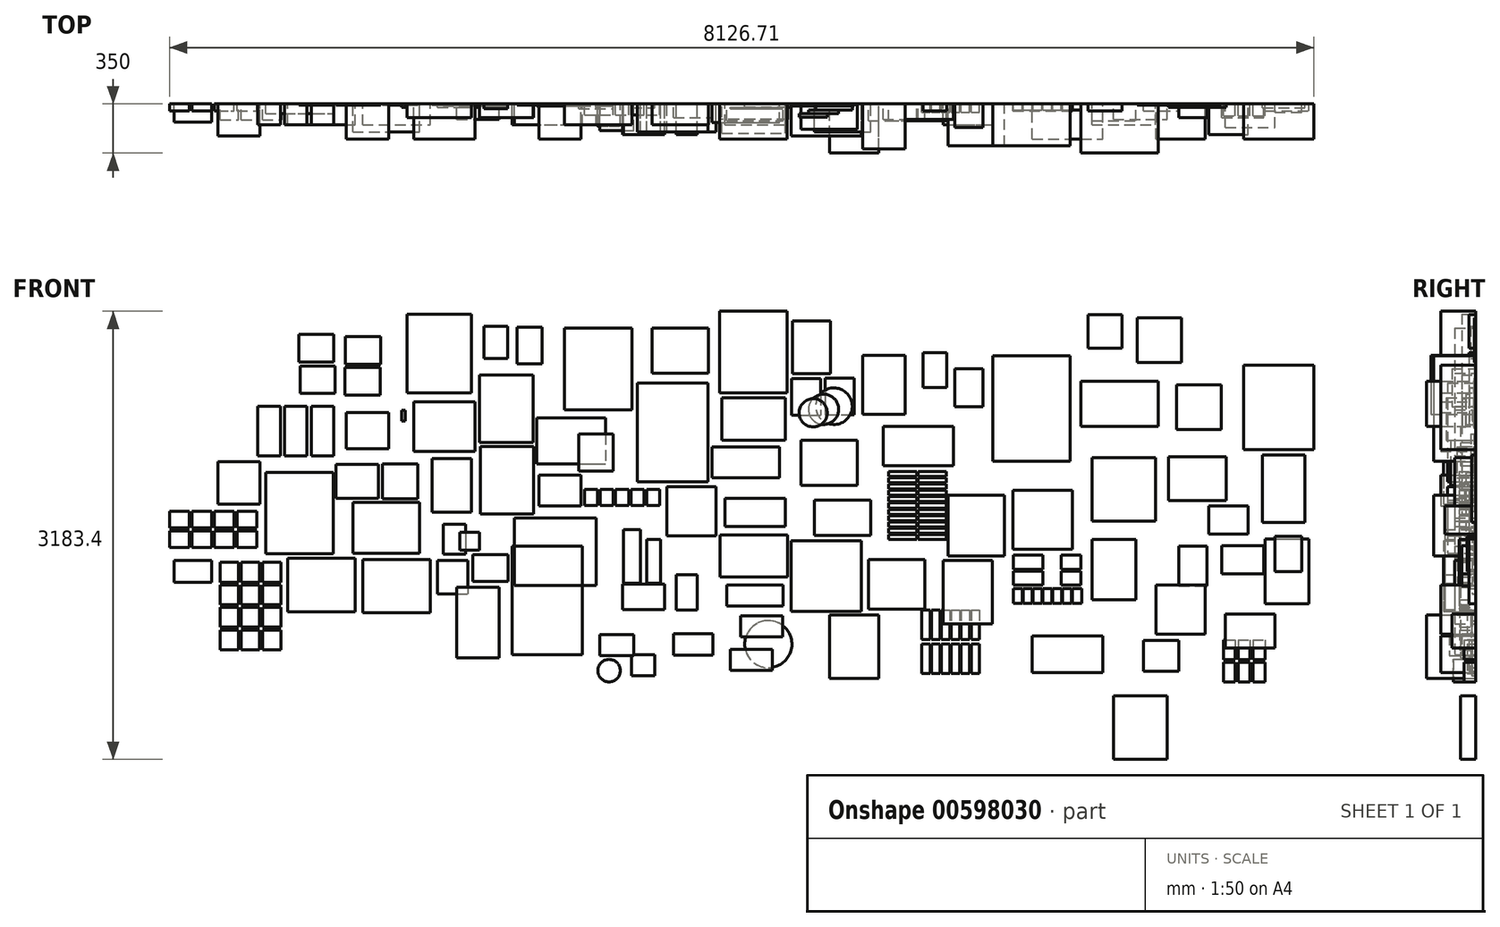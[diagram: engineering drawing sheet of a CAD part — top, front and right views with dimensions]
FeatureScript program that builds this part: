
annotation { "Feature Type Name" : "Feature", "Feature Type Description" : "" }
export const myFeature = defineFeature(function(context is Context, id is Id, definition is map)
    precondition{}
    {
        {
            var Q0;
            Q0=qCreatedBy(makeId("Front.planeOp"),FACE);
            var sketch = newSketch(context, id + "F0", { "sketchPlane" : qUnion([Q0])});
            skLineSegment(sketch, "E0.bottom", {"start": v(-280.76, 501.47) * mm, "end": v(269.24, 501.47) * mm});
            skLineSegment(sketch, "E0.top", {"start": v(-280.76, -248.53) * mm, "end": v(269.24, -248.53) * mm});
            skLineSegment(sketch, "E0.left", {"start": v(-280.76, 501.47) * mm, "end": v(-280.76, -248.53) * mm});
            skLineSegment(sketch, "E0.right", {"start": v(269.24, 501.47) * mm, "end": v(269.24, -248.53) * mm});
            skSolve(sketch);
        }
        {
            var Q0;
            Q0 = qSketchRegion(id + "F0", true);
            extrude(context, id + "F1", {"entities" : qUnion([Q0]), "depth" : 300 * mm, "offsetDistance" : 25 * mm});
        }
        {
            var Q0;
            Q0=qCreatedBy(makeId("Front.planeOp"),FACE);
            var sketch = newSketch(context, id + "F2", { "sketchPlane" : qUnion([Q0])});
            skLineSegment(sketch, "E1.bottom", {"start": v(-1059.28, 0) * mm, "end": v(-559.28, 0) * mm});
            skLineSegment(sketch, "E1.top", {"start": v(-1059.28, -280) * mm, "end": v(-559.28, -280) * mm});
            skLineSegment(sketch, "E1.left", {"start": v(-1059.28, 0) * mm, "end": v(-1059.28, -280) * mm});
            skLineSegment(sketch, "E1.right", {"start": v(-559.28, 0) * mm, "end": v(-559.28, -280) * mm});
            skSolve(sketch);
        }
        {
            var Q0;
            Q0=makeQuery(id+"F2.imprint","IMPRINT",FACE,{"disambiguationData":[TD([[makeQuery(id+"F2.imprint","IMPRINT",EDGE,{"derivedFrom":sQuery(id+"F2.wireOp",EDGE,"E1.bottom")}),-1.0]])]});
            extrude(context, id + "F3", {"entities" : qUnion([Q0]), "depth" : 110 * mm, "offsetDistance" : 25 * mm});
        }
        {
            var Q0;
            Q0=qCreatedBy(makeId("Front.planeOp"),FACE);
            var sketch = newSketch(context, id + "F4", { "sketchPlane" : qUnion([Q0])});
            skLineSegment(sketch, "E2.bottom", {"start": v(-1020.74, -769.84) * mm, "end": v(-820.74, -769.84) * mm});
            skLineSegment(sketch, "E2.top", {"start": v(-1020.74, -804.84) * mm, "end": v(-820.74, -804.84) * mm});
            skLineSegment(sketch, "E2.left", {"start": v(-1020.74, -769.84) * mm, "end": v(-1020.74, -804.84) * mm});
            skLineSegment(sketch, "E2.right", {"start": v(-820.74, -769.84) * mm, "end": v(-820.74, -804.84) * mm});
            skLineSegment(sketch, "E3.0.1.0", {"start": v(-1020.74, -724.84) * mm, "end": v(-1020.74, -759.84) * mm});
            skLineSegment(sketch, "E3.0.1.1", {"start": v(-1020.74, -759.84) * mm, "end": v(-820.74, -759.84) * mm});
            skLineSegment(sketch, "E3.0.1.2", {"start": v(-1020.74, -724.84) * mm, "end": v(-820.74, -724.84) * mm});
            skLineSegment(sketch, "E3.0.1.3", {"start": v(-820.74, -724.84) * mm, "end": v(-820.74, -759.84) * mm});
            skLineSegment(sketch, "E3.0.2.0", {"start": v(-1020.74, -679.84) * mm, "end": v(-1020.74, -714.84) * mm});
            skLineSegment(sketch, "E3.0.2.1", {"start": v(-1020.74, -714.84) * mm, "end": v(-820.74, -714.84) * mm});
            skLineSegment(sketch, "E3.0.2.2", {"start": v(-1020.74, -679.84) * mm, "end": v(-820.74, -679.84) * mm});
            skLineSegment(sketch, "E3.0.2.3", {"start": v(-820.74, -679.84) * mm, "end": v(-820.74, -714.84) * mm});
            skLineSegment(sketch, "E3.0.3.0", {"start": v(-1020.74, -634.84) * mm, "end": v(-1020.74, -669.84) * mm});
            skLineSegment(sketch, "E3.0.3.1", {"start": v(-1020.74, -669.84) * mm, "end": v(-820.74, -669.84) * mm});
            skLineSegment(sketch, "E3.0.3.2", {"start": v(-1020.74, -634.84) * mm, "end": v(-820.74, -634.84) * mm});
            skLineSegment(sketch, "E3.0.3.3", {"start": v(-820.74, -634.84) * mm, "end": v(-820.74, -669.84) * mm});
            skLineSegment(sketch, "E3.0.4.0", {"start": v(-1020.74, -589.84) * mm, "end": v(-1020.74, -624.84) * mm});
            skLineSegment(sketch, "E3.0.4.1", {"start": v(-1020.74, -624.84) * mm, "end": v(-820.74, -624.84) * mm});
            skLineSegment(sketch, "E3.0.4.2", {"start": v(-1020.74, -589.84) * mm, "end": v(-820.74, -589.84) * mm});
            skLineSegment(sketch, "E3.0.4.3", {"start": v(-820.74, -589.84) * mm, "end": v(-820.74, -624.84) * mm});
            skLineSegment(sketch, "E3.0.5.0", {"start": v(-1020.74, -544.84) * mm, "end": v(-1020.74, -579.84) * mm});
            skLineSegment(sketch, "E3.0.5.1", {"start": v(-1020.74, -579.84) * mm, "end": v(-820.74, -579.84) * mm});
            skLineSegment(sketch, "E3.0.5.2", {"start": v(-1020.74, -544.84) * mm, "end": v(-820.74, -544.84) * mm});
            skLineSegment(sketch, "E3.0.5.3", {"start": v(-820.74, -544.84) * mm, "end": v(-820.74, -579.84) * mm});
            skLineSegment(sketch, "E3.0.6.0", {"start": v(-1020.74, -499.84) * mm, "end": v(-1020.74, -534.84) * mm});
            skLineSegment(sketch, "E3.0.6.1", {"start": v(-1020.74, -534.84) * mm, "end": v(-820.74, -534.84) * mm});
            skLineSegment(sketch, "E3.0.6.2", {"start": v(-1020.74, -499.84) * mm, "end": v(-820.74, -499.84) * mm});
            skLineSegment(sketch, "E3.0.6.3", {"start": v(-820.74, -499.84) * mm, "end": v(-820.74, -534.84) * mm});
            skLineSegment(sketch, "E3.0.7.0", {"start": v(-1020.74, -454.84) * mm, "end": v(-1020.74, -489.84) * mm});
            skLineSegment(sketch, "E3.0.7.1", {"start": v(-1020.74, -489.84) * mm, "end": v(-820.74, -489.84) * mm});
            skLineSegment(sketch, "E3.0.7.2", {"start": v(-1020.74, -454.84) * mm, "end": v(-820.74, -454.84) * mm});
            skLineSegment(sketch, "E3.0.7.3", {"start": v(-820.74, -454.84) * mm, "end": v(-820.74, -489.84) * mm});
            skLineSegment(sketch, "E3.0.8.0", {"start": v(-1020.74, -409.84) * mm, "end": v(-1020.74, -444.84) * mm});
            skLineSegment(sketch, "E3.0.8.1", {"start": v(-1020.74, -444.84) * mm, "end": v(-820.74, -444.84) * mm});
            skLineSegment(sketch, "E3.0.8.2", {"start": v(-1020.74, -409.84) * mm, "end": v(-820.74, -409.84) * mm});
            skLineSegment(sketch, "E3.0.8.3", {"start": v(-820.74, -409.84) * mm, "end": v(-820.74, -444.84) * mm});
            skLineSegment(sketch, "E3.0.9.0", {"start": v(-1020.74, -364.84) * mm, "end": v(-1020.74, -399.84) * mm});
            skLineSegment(sketch, "E3.0.9.1", {"start": v(-1020.74, -399.84) * mm, "end": v(-820.74, -399.84) * mm});
            skLineSegment(sketch, "E3.0.9.2", {"start": v(-1020.74, -364.84) * mm, "end": v(-820.74, -364.84) * mm});
            skLineSegment(sketch, "E3.0.9.3", {"start": v(-820.74, -364.84) * mm, "end": v(-820.74, -399.84) * mm});
            skLineSegment(sketch, "E3.0.10.0", {"start": v(-1020.74, -319.84) * mm, "end": v(-1020.74, -354.84) * mm});
            skLineSegment(sketch, "E3.0.10.1", {"start": v(-1020.74, -354.84) * mm, "end": v(-820.74, -354.84) * mm});
            skLineSegment(sketch, "E3.0.10.2", {"start": v(-1020.74, -319.84) * mm, "end": v(-820.74, -319.84) * mm});
            skLineSegment(sketch, "E3.0.10.3", {"start": v(-820.74, -319.84) * mm, "end": v(-820.74, -354.84) * mm});
            skLineSegment(sketch, "E3.1.0.0", {"start": v(-810.74, -769.84) * mm, "end": v(-810.74, -804.84) * mm});
            skLineSegment(sketch, "E3.1.0.1", {"start": v(-810.74, -804.84) * mm, "end": v(-610.74, -804.84) * mm});
            skLineSegment(sketch, "E3.1.0.2", {"start": v(-810.74, -769.84) * mm, "end": v(-610.74, -769.84) * mm});
            skLineSegment(sketch, "E3.1.0.3", {"start": v(-610.74, -769.84) * mm, "end": v(-610.74, -804.84) * mm});
            skLineSegment(sketch, "E3.1.1.0", {"start": v(-810.74, -724.84) * mm, "end": v(-810.74, -759.84) * mm});
            skLineSegment(sketch, "E3.1.1.1", {"start": v(-810.74, -759.84) * mm, "end": v(-610.74, -759.84) * mm});
            skLineSegment(sketch, "E3.1.1.2", {"start": v(-810.74, -724.84) * mm, "end": v(-610.74, -724.84) * mm});
            skLineSegment(sketch, "E3.1.1.3", {"start": v(-610.74, -724.84) * mm, "end": v(-610.74, -759.84) * mm});
            skLineSegment(sketch, "E3.1.2.0", {"start": v(-810.74, -679.84) * mm, "end": v(-810.74, -714.84) * mm});
            skLineSegment(sketch, "E3.1.2.1", {"start": v(-810.74, -714.84) * mm, "end": v(-610.74, -714.84) * mm});
            skLineSegment(sketch, "E3.1.2.2", {"start": v(-810.74, -679.84) * mm, "end": v(-610.74, -679.84) * mm});
            skLineSegment(sketch, "E3.1.2.3", {"start": v(-610.74, -679.84) * mm, "end": v(-610.74, -714.84) * mm});
            skLineSegment(sketch, "E3.1.3.0", {"start": v(-810.74, -634.84) * mm, "end": v(-810.74, -669.84) * mm});
            skLineSegment(sketch, "E3.1.3.1", {"start": v(-810.74, -669.84) * mm, "end": v(-610.74, -669.84) * mm});
            skLineSegment(sketch, "E3.1.3.2", {"start": v(-810.74, -634.84) * mm, "end": v(-610.74, -634.84) * mm});
            skLineSegment(sketch, "E3.1.3.3", {"start": v(-610.74, -634.84) * mm, "end": v(-610.74, -669.84) * mm});
            skLineSegment(sketch, "E3.1.4.0", {"start": v(-810.74, -589.84) * mm, "end": v(-810.74, -624.84) * mm});
            skLineSegment(sketch, "E3.1.4.1", {"start": v(-810.74, -624.84) * mm, "end": v(-610.74, -624.84) * mm});
            skLineSegment(sketch, "E3.1.4.2", {"start": v(-810.74, -589.84) * mm, "end": v(-610.74, -589.84) * mm});
            skLineSegment(sketch, "E3.1.4.3", {"start": v(-610.74, -589.84) * mm, "end": v(-610.74, -624.84) * mm});
            skLineSegment(sketch, "E3.1.5.0", {"start": v(-810.74, -544.84) * mm, "end": v(-810.74, -579.84) * mm});
            skLineSegment(sketch, "E3.1.5.1", {"start": v(-810.74, -579.84) * mm, "end": v(-610.74, -579.84) * mm});
            skLineSegment(sketch, "E3.1.5.2", {"start": v(-810.74, -544.84) * mm, "end": v(-610.74, -544.84) * mm});
            skLineSegment(sketch, "E3.1.5.3", {"start": v(-610.74, -544.84) * mm, "end": v(-610.74, -579.84) * mm});
            skLineSegment(sketch, "E3.1.6.0", {"start": v(-810.74, -499.84) * mm, "end": v(-810.74, -534.84) * mm});
            skLineSegment(sketch, "E3.1.6.1", {"start": v(-810.74, -534.84) * mm, "end": v(-610.74, -534.84) * mm});
            skLineSegment(sketch, "E3.1.6.2", {"start": v(-810.74, -499.84) * mm, "end": v(-610.74, -499.84) * mm});
            skLineSegment(sketch, "E3.1.6.3", {"start": v(-610.74, -499.84) * mm, "end": v(-610.74, -534.84) * mm});
            skLineSegment(sketch, "E3.1.7.0", {"start": v(-810.74, -454.84) * mm, "end": v(-810.74, -489.84) * mm});
            skLineSegment(sketch, "E3.1.7.1", {"start": v(-810.74, -489.84) * mm, "end": v(-610.74, -489.84) * mm});
            skLineSegment(sketch, "E3.1.7.2", {"start": v(-810.74, -454.84) * mm, "end": v(-610.74, -454.84) * mm});
            skLineSegment(sketch, "E3.1.7.3", {"start": v(-610.74, -454.84) * mm, "end": v(-610.74, -489.84) * mm});
            skLineSegment(sketch, "E3.1.8.0", {"start": v(-810.74, -409.84) * mm, "end": v(-810.74, -444.84) * mm});
            skLineSegment(sketch, "E3.1.8.1", {"start": v(-810.74, -444.84) * mm, "end": v(-610.74, -444.84) * mm});
            skLineSegment(sketch, "E3.1.8.2", {"start": v(-810.74, -409.84) * mm, "end": v(-610.74, -409.84) * mm});
            skLineSegment(sketch, "E3.1.8.3", {"start": v(-610.74, -409.84) * mm, "end": v(-610.74, -444.84) * mm});
            skLineSegment(sketch, "E3.1.9.0", {"start": v(-810.74, -364.84) * mm, "end": v(-810.74, -399.84) * mm});
            skLineSegment(sketch, "E3.1.9.1", {"start": v(-810.74, -399.84) * mm, "end": v(-610.74, -399.84) * mm});
            skLineSegment(sketch, "E3.1.9.2", {"start": v(-810.74, -364.84) * mm, "end": v(-610.74, -364.84) * mm});
            skLineSegment(sketch, "E3.1.9.3", {"start": v(-610.74, -364.84) * mm, "end": v(-610.74, -399.84) * mm});
            skLineSegment(sketch, "E3.1.10.0", {"start": v(-810.74, -319.84) * mm, "end": v(-810.74, -354.84) * mm});
            skLineSegment(sketch, "E3.1.10.1", {"start": v(-810.74, -354.84) * mm, "end": v(-610.74, -354.84) * mm});
            skLineSegment(sketch, "E3.1.10.2", {"start": v(-810.74, -319.84) * mm, "end": v(-610.74, -319.84) * mm});
            skLineSegment(sketch, "E3.1.10.3", {"start": v(-610.74, -319.84) * mm, "end": v(-610.74, -354.84) * mm});
            skLineSegment(sketch, "E3.direction1", {"start": v(-1020.74, -804.84) * mm, "end": v(-810.74, -804.84) * mm, "construction": true});
            skLineSegment(sketch, "E3.direction2", {"start": v(-1020.74, -804.84) * mm, "end": v(-1020.74, -759.84) * mm, "construction": true});
            skSolve(sketch);
        }
        {
            var Q0;
            Q0 = qSketchRegion(id + "F4", true);
            extrude(context, id + "F5", {"entities" : qUnion([Q0]), "depth" : 120 * mm, "offsetDistance" : 25 * mm});
        }
        {
            var Q0;
            Q0=qCreatedBy(makeId("Front.planeOp"),FACE);
            var sketch = newSketch(context, id + "F6", { "sketchPlane" : qUnion([Q0])});
            skLineSegment(sketch, "E4.bottom", {"start": v(345.58, 320) * mm, "end": v(895.58, 320) * mm});
            skLineSegment(sketch, "E4.top", {"start": v(345.58, 0) * mm, "end": v(895.58, 0) * mm});
            skLineSegment(sketch, "E4.left", {"start": v(345.58, 320) * mm, "end": v(345.58, 0) * mm});
            skLineSegment(sketch, "E4.right", {"start": v(895.58, 320) * mm, "end": v(895.58, 0) * mm});
            skSolve(sketch);
        }
        {
            var Q0;
            Q0 = qSketchRegion(id + "F6", true);
            extrude(context, id + "F7", {"entities" : qUnion([Q0]), "depth" : 350 * mm, "offsetDistance" : 25 * mm});
        }
        {
            var Q0;
            Q0=qCreatedBy(makeId("Front.planeOp"),FACE);
            var sketch = newSketch(context, id + "F8", { "sketchPlane" : qUnion([Q0])});
            skLineSegment(sketch, "E5.bottom", {"start": v(-135.88, -452.91) * mm, "end": v(284.12, -452.91) * mm});
            skLineSegment(sketch, "E5.top", {"start": v(-135.88, -872.91) * mm, "end": v(284.12, -872.91) * mm});
            skLineSegment(sketch, "E5.left", {"start": v(-135.88, -452.91) * mm, "end": v(-135.88, -872.91) * mm});
            skLineSegment(sketch, "E5.right", {"start": v(284.12, -452.91) * mm, "end": v(284.12, -872.91) * mm});
            skSolve(sketch);
        }
        {
            var Q0;
            Q0 = qSketchRegion(id + "F8", true);
            extrude(context, id + "F9", {"entities" : qUnion([Q0]), "depth" : 50 * mm, "offsetDistance" : 25 * mm});
        }
        {
            var Q0;
            Q0=qCreatedBy(makeId("Front.planeOp"),FACE);
            var sketch = newSketch(context, id + "F10", { "sketchPlane" : qUnion([Q0])});
            skLineSegment(sketch, "E6.bottom", {"start": v(424.42, -222.7) * mm, "end": v(874.42, -222.7) * mm});
            skLineSegment(sketch, "E6.top", {"start": v(424.42, -672.7) * mm, "end": v(874.42, -672.7) * mm});
            skLineSegment(sketch, "E6.left", {"start": v(424.42, -222.7) * mm, "end": v(424.42, -672.7) * mm});
            skLineSegment(sketch, "E6.right", {"start": v(874.42, -222.7) * mm, "end": v(874.42, -672.7) * mm});
            skSolve(sketch);
        }
        {
            var Q0;
            Q0 = qSketchRegion(id + "F10", true);
            extrude(context, id + "F11", {"entities" : qUnion([Q0]), "depth" : 150 * mm, "offsetDistance" : 25 * mm});
        }
        {
            var Q0;
            Q0=qCreatedBy(makeId("Front.planeOp"),FACE);
            var sketch = newSketch(context, id + "F12", { "sketchPlane" : qUnion([Q0])});
            skLineSegment(sketch, "E7.bottom", {"start": v(-596.95, -490.51) * mm, "end": v(-196.95, -490.51) * mm});
            skLineSegment(sketch, "E7.top", {"start": v(-596.95, -920.51) * mm, "end": v(-196.95, -920.51) * mm});
            skLineSegment(sketch, "E7.left", {"start": v(-596.95, -490.51) * mm, "end": v(-596.95, -920.51) * mm});
            skLineSegment(sketch, "E7.right", {"start": v(-196.95, -490.51) * mm, "end": v(-196.95, -920.51) * mm});
            skSolve(sketch);
        }
        {
            var Q0;
            Q0 = qSketchRegion(id + "F12", true);
            extrude(context, id + "F13", {"entities" : qUnion([Q0]), "depth" : 300 * mm, "offsetDistance" : 25 * mm});
        }
        {
            var Q0;
            Q0=qCreatedBy(makeId("Front.planeOp"),FACE);
            var sketch = newSketch(context, id + "F14", { "sketchPlane" : qUnion([Q0])});
            skLineSegment(sketch, "E8.bottom", {"start": v(425.31, -802.48) * mm, "end": v(735.31, -802.48) * mm});
            skLineSegment(sketch, "E8.top", {"start": v(425.31, -1232.48) * mm, "end": v(735.31, -1232.48) * mm});
            skLineSegment(sketch, "E8.left", {"start": v(425.31, -802.48) * mm, "end": v(425.31, -1232.48) * mm});
            skLineSegment(sketch, "E8.right", {"start": v(735.31, -802.48) * mm, "end": v(735.31, -1232.48) * mm});
            skSolve(sketch);
        }
        {
            var Q0;
            Q0 = qSketchRegion(id + "F14", true);
            extrude(context, id + "F15", {"entities" : qUnion([Q0]), "depth" : 120 * mm, "offsetDistance" : 25 * mm});
        }
        {
            var Q0;
            Q0=qCreatedBy(makeId("Front.planeOp"),FACE);
            var sketch = newSketch(context, id + "F16", { "sketchPlane" : qUnion([Q0])});
            skLineSegment(sketch, "E9.bottom", {"start": v(-1162.4, -947.76) * mm, "end": v(-762.4, -947.76) * mm});
            skLineSegment(sketch, "E9.top", {"start": v(-1162.4, -1297.76) * mm, "end": v(-762.4, -1297.76) * mm});
            skLineSegment(sketch, "E9.left", {"start": v(-1162.4, -947.76) * mm, "end": v(-1162.4, -1297.76) * mm});
            skLineSegment(sketch, "E9.right", {"start": v(-762.4, -947.76) * mm, "end": v(-762.4, -1297.76) * mm});
            skSolve(sketch);
        }
        {
            var Q0;
            Q0 = qSketchRegion(id + "F16", true);
            extrude(context, id + "F17", {"entities" : qUnion([Q0]), "depth" : 120 * mm, "offsetDistance" : 25 * mm});
        }
        {
            var Q0;
            Q0=qCreatedBy(makeId("Front.planeOp"),FACE);
            var sketch = newSketch(context, id + "F18", { "sketchPlane" : qUnion([Q0])});
            skLineSegment(sketch, "E10.bottom", {"start": v(-776.5, 524.74) * mm, "end": v(-606.5, 524.74) * mm});
            skLineSegment(sketch, "E10.top", {"start": v(-776.5, 274.74) * mm, "end": v(-606.5, 274.74) * mm});
            skLineSegment(sketch, "E10.left", {"start": v(-776.5, 524.74) * mm, "end": v(-776.5, 274.74) * mm});
            skLineSegment(sketch, "E10.right", {"start": v(-606.5, 524.74) * mm, "end": v(-606.5, 274.74) * mm});
            skSolve(sketch);
        }
        {
            var Q0;
            Q0 = qSketchRegion(id + "F18", true);
            extrude(context, id + "F19", {"entities" : qUnion([Q0]), "depth" : 50 * mm, "offsetDistance" : 25 * mm});
        }
        {
            var Q0;
            Q0=qCreatedBy(makeId("Front.planeOp"),FACE);
            var sketch = newSketch(context, id + "F20", { "sketchPlane" : qUnion([Q0])});
            skLineSegment(sketch, "E11.bottom", {"start": v(-549.3, 409.47) * mm, "end": v(-349.3, 409.47) * mm});
            skLineSegment(sketch, "E11.top", {"start": v(-549.3, 139.47) * mm, "end": v(-349.3, 139.47) * mm});
            skLineSegment(sketch, "E11.left", {"start": v(-549.3, 409.47) * mm, "end": v(-549.3, 139.47) * mm});
            skLineSegment(sketch, "E11.right", {"start": v(-349.3, 409.47) * mm, "end": v(-349.3, 139.47) * mm});
            skSolve(sketch);
        }
        {
            var Q0;
            Q0 = qSketchRegion(id + "F20", true);
            extrude(context, id + "F21", {"entities" : qUnion([Q0]), "depth" : 170 * mm, "offsetDistance" : 25 * mm});
        }
        {
            var Q0;
            Q0=qCreatedBy(makeId("Front.planeOp"),FACE);
            var sketch = newSketch(context, id + "F22", { "sketchPlane" : qUnion([Q0])});
            skLineSegment(sketch, "E12.bottom", {"start": v(-1643, -98.18) * mm, "end": v(-1243, -98.18) * mm});
            skLineSegment(sketch, "E12.top", {"start": v(-1643, -418.18) * mm, "end": v(-1243, -418.18) * mm});
            skLineSegment(sketch, "E12.left", {"start": v(-1643, -98.18) * mm, "end": v(-1643, -418.18) * mm});
            skLineSegment(sketch, "E12.right", {"start": v(-1243, -98.18) * mm, "end": v(-1243, -418.18) * mm});
            skSolve(sketch);
        }
        {
            var Q0;
            Q0 = qSketchRegion(id + "F22", true);
            extrude(context, id + "F23", {"entities" : qUnion([Q0]), "depth" : 180 * mm, "offsetDistance" : 25 * mm});
        }
        {
            var Q0;
            Q0=qCreatedBy(makeId("Front.planeOp"),FACE);
            var sketch = newSketch(context, id + "F24", { "sketchPlane" : qUnion([Q0])});
            skLineSegment(sketch, "E13.bottom", {"start": v(-1548.03, -523.96) * mm, "end": v(-1148.03, -523.96) * mm});
            skLineSegment(sketch, "E13.top", {"start": v(-1548.03, -773.96) * mm, "end": v(-1148.03, -773.96) * mm});
            skLineSegment(sketch, "E13.left", {"start": v(-1548.03, -523.96) * mm, "end": v(-1548.03, -773.96) * mm});
            skLineSegment(sketch, "E13.right", {"start": v(-1148.03, -523.96) * mm, "end": v(-1148.03, -773.96) * mm});
            skSolve(sketch);
        }
        {
            var Q0;
            Q0 = qSketchRegion(id + "F24", true);
            extrude(context, id + "F25", {"entities" : qUnion([Q0]), "depth" : 200 * mm, "offsetDistance" : 25 * mm});
        }
        {
            var Q0;
            Q0=qCreatedBy(makeId("Front.planeOp"),FACE);
            var sketch = newSketch(context, id + "F26", { "sketchPlane" : qUnion([Q0])});
            skLineSegment(sketch, "E14.bottom", {"start": v(-1203.06, 505.03) * mm, "end": v(-903.06, 505.03) * mm});
            skLineSegment(sketch, "E14.top", {"start": v(-1203.06, 85.03) * mm, "end": v(-903.06, 85.03) * mm});
            skLineSegment(sketch, "E14.left", {"start": v(-1203.06, 505.03) * mm, "end": v(-1203.06, 85.03) * mm});
            skLineSegment(sketch, "E14.right", {"start": v(-903.06, 505.03) * mm, "end": v(-903.06, 85.03) * mm});
            skSolve(sketch);
        }
        {
            var Q0;
            Q0 = qSketchRegion(id + "F26", true);
            extrude(context, id + "F27", {"entities" : qUnion([Q0]), "depth" : 320 * mm, "offsetDistance" : 25 * mm});
        }
        {
            var Q0;
            Q0=qCreatedBy(makeId("Front.planeOp"),FACE);
            var sketch = newSketch(context, id + "F28", { "sketchPlane" : qUnion([Q0])});
            skLineSegment(sketch, "E15.bottom", {"start": v(-1470.81, 341.37) * mm, "end": v(-1265.81, 341.37) * mm});
            skLineSegment(sketch, "E15.top", {"start": v(-1470.81, 81.37) * mm, "end": v(-1265.81, 81.37) * mm});
            skLineSegment(sketch, "E15.left", {"start": v(-1470.81, 341.37) * mm, "end": v(-1470.81, 81.37) * mm});
            skLineSegment(sketch, "E15.right", {"start": v(-1265.81, 341.37) * mm, "end": v(-1265.81, 81.37) * mm});
            skLineSegment(sketch, "E16.bottom", {"start": v(-1707.86, 339.1) * mm, "end": v(-1502.86, 339.1) * mm});
            skLineSegment(sketch, "E16.top", {"start": v(-1707.86, 79.1) * mm, "end": v(-1502.86, 79.1) * mm});
            skLineSegment(sketch, "E16.left", {"start": v(-1707.86, 339.1) * mm, "end": v(-1707.86, 79.1) * mm});
            skLineSegment(sketch, "E16.right", {"start": v(-1502.86, 339.1) * mm, "end": v(-1502.86, 79.1) * mm});
            skSolve(sketch);
        }
        {
            var Q0;
            Q0 = qSketchRegion(id + "F28", true);
            extrude(context, id + "F29", {"entities" : qUnion([Q0]), "depth" : 15 * mm, "offsetDistance" : 25 * mm});
        }
        {
            var Q0;
            Q0=makeQuery(id+"F29.opExtrude","CAP_FACE",FACE,{"disambiguationData":[OSD([sQuery(id+"F28.wireOp",EDGE,"E15.bottom"),sQuery(id+"F28.wireOp",EDGE,"E15.top"),sQuery(id+"F28.wireOp",EDGE,"E15.left"),sQuery(id+"F28.wireOp",EDGE,"E15.right")])],"isStart":false});
            var sketch = newSketch(context, id + "F30", { "sketchPlane" : qUnion([Q0])});
            skCircle(sketch, "E17", {"center": v(-1407.86, 143.14) * mm, "radius": 130 * mm});
            skSolve(sketch);
        }
        {
            var Q0;
            Q0 = qSketchRegion(id + "F30", true);
            extrude(context, id + "F31", {"entities" : qUnion([Q0]), "depth" : 30 * mm, "offsetDistance" : 25 * mm});
        }
        {
            var Q0;
            Q0=makeQuery(id+"F31.opExtrude","CAP_FACE",FACE,{"disambiguationData":[OSD([sQuery(id+"F30.wireOp",EDGE,"E17")])],"isStart":false});
            var sketch = newSketch(context, id + "F32", { "sketchPlane" : qUnion([Q0])});
            skCircle(sketch, "E18", {"center": v(-1481.46, 120.94) * mm, "radius": 107.5 * mm});
            skSolve(sketch);
        }
        {
            var Q0;
            Q0 = qSketchRegion(id + "F32", true);
            extrude(context, id + "F33", {"entities" : qUnion([Q0]), "operationType" : NewBodyOperationType.ADD, "depth" : 25 * mm, "offsetDistance" : 25 * mm});
        }
        {
            var Q0;
            Q0=makeQuery(id+"F33.opExtrude","CAP_FACE",FACE,{"disambiguationData":[OSD([sQuery(id+"F32.wireOp",EDGE,"E18")])],"isStart":false});
            var sketch = newSketch(context, id + "F34", { "sketchPlane" : qUnion([Q0])});
            skCircle(sketch, "E19", {"center": v(-1555.29, 96.33) * mm, "radius": 100 * mm});
            skSolve(sketch);
        }
        {
            var Q0;
            Q0 = qSketchRegion(id + "F34", true);
            extrude(context, id + "F35", {"entities" : qUnion([Q0]), "operationType" : NewBodyOperationType.ADD, "depth" : 25 * mm, "offsetDistance" : 25 * mm});
        }
        {
            var Q0;
            Q0=qCreatedBy(makeId("Front.planeOp"),FACE);
            var sketch = newSketch(context, id + "F36", { "sketchPlane" : qUnion([Q0])});
            skLineSegment(sketch, "E20.bottom", {"start": v(-1712.3, -814.65) * mm, "end": v(-1212.3, -814.65) * mm});
            skLineSegment(sketch, "E20.top", {"start": v(-1712.3, -1314.65) * mm, "end": v(-1212.3, -1314.65) * mm});
            skLineSegment(sketch, "E20.left", {"start": v(-1712.3, -814.65) * mm, "end": v(-1712.3, -1314.65) * mm});
            skLineSegment(sketch, "E20.right", {"start": v(-1212.3, -814.65) * mm, "end": v(-1212.3, -1314.65) * mm});
            skSolve(sketch);
        }
        {
            var Q0;
            Q0 = qSketchRegion(id + "F36", true);
            extrude(context, id + "F37", {"entities" : qUnion([Q0]), "depth" : 230 * mm, "offsetDistance" : 25 * mm});
        }
        {
            var Q0;
            Q0=qCreatedBy(makeId("Front.planeOp"),FACE);
            var sketch = newSketch(context, id + "F38", { "sketchPlane" : qUnion([Q0])});
            skLineSegment(sketch, "E21.bottom", {"start": v(-2181.74, -512.18) * mm, "end": v(-1751.74, -512.18) * mm});
            skLineSegment(sketch, "E21.top", {"start": v(-2181.74, -712.18) * mm, "end": v(-1751.74, -712.18) * mm});
            skLineSegment(sketch, "E21.left", {"start": v(-2181.74, -512.18) * mm, "end": v(-2181.74, -712.18) * mm});
            skLineSegment(sketch, "E21.right", {"start": v(-1751.74, -512.18) * mm, "end": v(-1751.74, -712.18) * mm});
            skSolve(sketch);
        }
        {
            var Q0;
            Q0 = qSketchRegion(id + "F38", true);
            extrude(context, id + "F39", {"entities" : qUnion([Q0]), "depth" : 150 * mm, "offsetDistance" : 25 * mm});
        }
        {
            var Q0;
            Q0=qCreatedBy(makeId("Front.planeOp"),FACE);
            var sketch = newSketch(context, id + "F40", { "sketchPlane" : qUnion([Q0])});
            skLineSegment(sketch, "E22.bottom", {"start": v(-632.02, -952.32) * mm, "end": v(-282.02, -952.32) * mm});
            skLineSegment(sketch, "E22.top", {"start": v(-632.02, -1402.32) * mm, "end": v(-282.02, -1402.32) * mm});
            skLineSegment(sketch, "E22.left", {"start": v(-632.02, -952.32) * mm, "end": v(-632.02, -1402.32) * mm});
            skLineSegment(sketch, "E22.right", {"start": v(-282.02, -952.32) * mm, "end": v(-282.02, -1402.32) * mm});
            skSolve(sketch);
        }
        {
            var Q0;
            Q0 = qSketchRegion(id + "F40", true);
            extrude(context, id + "F41", {"entities" : qUnion([Q0]), "depth" : 150 * mm, "offsetDistance" : 25 * mm});
        }
        {
            var Q0;
            Q0=qCreatedBy(makeId("Front.planeOp"),FACE);
            var sketch = newSketch(context, id + "F42", { "sketchPlane" : qUnion([Q0])});
            skLineSegment(sketch, "E23.bottom", {"start": v(-134.68, -915.74) * mm, "end": v(75.32, -915.74) * mm});
            skLineSegment(sketch, "E23.top", {"start": v(-134.68, -1015.74) * mm, "end": v(75.32, -1015.74) * mm});
            skLineSegment(sketch, "E23.left", {"start": v(-134.68, -915.74) * mm, "end": v(-134.68, -1015.74) * mm});
            skLineSegment(sketch, "E23.right", {"start": v(75.32, -915.74) * mm, "end": v(75.32, -1015.74) * mm});
            skLineSegment(sketch, "E24.bottom", {"start": v(-134.68, -1029.07) * mm, "end": v(75.32, -1029.07) * mm});
            skLineSegment(sketch, "E24.top", {"start": v(-134.68, -1129.07) * mm, "end": v(75.32, -1129.07) * mm});
            skLineSegment(sketch, "E24.left", {"start": v(-134.68, -1029.07) * mm, "end": v(-134.68, -1129.07) * mm});
            skLineSegment(sketch, "E24.right", {"start": v(75.32, -1029.07) * mm, "end": v(75.32, -1129.07) * mm});
            skLineSegment(sketch, "E25.bottom", {"start": v(205.9, -915.74) * mm, "end": v(345.9, -915.74) * mm});
            skLineSegment(sketch, "E25.top", {"start": v(205.9, -1015.74) * mm, "end": v(345.9, -1015.74) * mm});
            skLineSegment(sketch, "E25.left", {"start": v(205.9, -915.74) * mm, "end": v(205.9, -1015.74) * mm});
            skLineSegment(sketch, "E25.right", {"start": v(345.9, -915.74) * mm, "end": v(345.9, -1015.74) * mm});
            skLineSegment(sketch, "E26.bottom", {"start": v(205.9, -1029.07) * mm, "end": v(345.9, -1029.07) * mm});
            skLineSegment(sketch, "E26.top", {"start": v(205.9, -1129.07) * mm, "end": v(345.9, -1129.07) * mm});
            skLineSegment(sketch, "E26.left", {"start": v(205.9, -1029.07) * mm, "end": v(205.9, -1129.07) * mm});
            skLineSegment(sketch, "E26.right", {"start": v(345.9, -1029.07) * mm, "end": v(345.9, -1129.07) * mm});
            skLineSegment(sketch, "E27.bottom", {"start": v(-134.68, -1151.47) * mm, "end": v(-69.68, -1151.47) * mm});
            skLineSegment(sketch, "E27.top", {"start": v(-134.68, -1256.47) * mm, "end": v(-69.68, -1256.47) * mm});
            skLineSegment(sketch, "E27.left", {"start": v(-134.68, -1151.47) * mm, "end": v(-134.68, -1256.47) * mm});
            skLineSegment(sketch, "E27.right", {"start": v(-69.68, -1151.47) * mm, "end": v(-69.68, -1256.47) * mm});
            skLineSegment(sketch, "E28.1.0.0", {"start": v(-64.68, -1151.47) * mm, "end": v(0.32, -1151.47) * mm});
            skLineSegment(sketch, "E28.1.0.1", {"start": v(-64.68, -1256.47) * mm, "end": v(0.32, -1256.47) * mm});
            skLineSegment(sketch, "E28.1.0.2", {"start": v(-64.68, -1151.47) * mm, "end": v(-64.68, -1256.47) * mm});
            skLineSegment(sketch, "E28.1.0.3", {"start": v(0.32, -1151.47) * mm, "end": v(0.32, -1256.47) * mm});
            skLineSegment(sketch, "E28.2.0.0", {"start": v(5.32, -1151.47) * mm, "end": v(70.32, -1151.47) * mm});
            skLineSegment(sketch, "E28.2.0.1", {"start": v(5.32, -1256.47) * mm, "end": v(70.32, -1256.47) * mm});
            skLineSegment(sketch, "E28.2.0.2", {"start": v(5.32, -1151.47) * mm, "end": v(5.32, -1256.47) * mm});
            skLineSegment(sketch, "E28.2.0.3", {"start": v(70.32, -1151.47) * mm, "end": v(70.32, -1256.47) * mm});
            skLineSegment(sketch, "E28.3.0.0", {"start": v(75.32, -1151.47) * mm, "end": v(140.32, -1151.47) * mm});
            skLineSegment(sketch, "E28.3.0.1", {"start": v(75.32, -1256.47) * mm, "end": v(140.32, -1256.47) * mm});
            skLineSegment(sketch, "E28.3.0.2", {"start": v(75.32, -1151.47) * mm, "end": v(75.32, -1256.47) * mm});
            skLineSegment(sketch, "E28.3.0.3", {"start": v(140.32, -1151.47) * mm, "end": v(140.32, -1256.47) * mm});
            skLineSegment(sketch, "E28.4.0.0", {"start": v(145.32, -1151.47) * mm, "end": v(210.32, -1151.47) * mm});
            skLineSegment(sketch, "E28.4.0.1", {"start": v(145.32, -1256.47) * mm, "end": v(210.32, -1256.47) * mm});
            skLineSegment(sketch, "E28.4.0.2", {"start": v(145.32, -1151.47) * mm, "end": v(145.32, -1256.47) * mm});
            skLineSegment(sketch, "E28.4.0.3", {"start": v(210.32, -1151.47) * mm, "end": v(210.32, -1256.47) * mm});
            skLineSegment(sketch, "E28.5.0.0", {"start": v(215.32, -1151.47) * mm, "end": v(280.32, -1151.47) * mm});
            skLineSegment(sketch, "E28.5.0.1", {"start": v(215.32, -1256.47) * mm, "end": v(280.32, -1256.47) * mm});
            skLineSegment(sketch, "E28.5.0.2", {"start": v(215.32, -1151.47) * mm, "end": v(215.32, -1256.47) * mm});
            skLineSegment(sketch, "E28.5.0.3", {"start": v(280.32, -1151.47) * mm, "end": v(280.32, -1256.47) * mm});
            skLineSegment(sketch, "E28.6.0.0", {"start": v(285.32, -1151.47) * mm, "end": v(350.32, -1151.47) * mm});
            skLineSegment(sketch, "E28.6.0.1", {"start": v(285.32, -1256.47) * mm, "end": v(350.32, -1256.47) * mm});
            skLineSegment(sketch, "E28.6.0.2", {"start": v(285.32, -1151.47) * mm, "end": v(285.32, -1256.47) * mm});
            skLineSegment(sketch, "E28.6.0.3", {"start": v(350.32, -1151.47) * mm, "end": v(350.32, -1256.47) * mm});
            skLineSegment(sketch, "E28.direction1", {"start": v(-134.68, -1256.47) * mm, "end": v(-64.68, -1256.47) * mm, "construction": true});
            skSolve(sketch);
        }
        {
            var Q0;
            Q0=makeQuery(id+"F42.imprint","IMPRINT",FACE,{"disambiguationData":[TD([[makeQuery(id+"F42.imprint","IMPRINT",EDGE,{"derivedFrom":sQuery(id+"F42.wireOp",EDGE,"E23.bottom")}),-1.0]])]});
            var Q1;
            Q1=makeQuery(id+"F42.imprint","IMPRINT",FACE,{"disambiguationData":[TD([[makeQuery(id+"F42.imprint","IMPRINT",EDGE,{"derivedFrom":sQuery(id+"F42.wireOp",EDGE,"E24.bottom")}),-1.0]])]});
            var Q2;
            Q2=makeQuery(id+"F42.imprint","IMPRINT",FACE,{"disambiguationData":[TD([[makeQuery(id+"F42.imprint","IMPRINT",EDGE,{"derivedFrom":sQuery(id+"F42.wireOp",EDGE,"E27.bottom")}),-1.0]])]});
            var Q3;
            Q3=makeQuery(id+"F42.imprint","IMPRINT",FACE,{"disambiguationData":[TD([[makeQuery(id+"F42.imprint","IMPRINT",EDGE,{"derivedFrom":sQuery(id+"F42.wireOp",EDGE,"E28.1.0.0")}),-1.0]])]});
            var Q4;
            Q4=makeQuery(id+"F42.imprint","IMPRINT",FACE,{"disambiguationData":[TD([[makeQuery(id+"F42.imprint","IMPRINT",EDGE,{"derivedFrom":sQuery(id+"F42.wireOp",EDGE,"E28.2.0.0")}),-1.0]])]});
            var Q5;
            Q5=makeQuery(id+"F42.imprint","IMPRINT",FACE,{"disambiguationData":[TD([[makeQuery(id+"F42.imprint","IMPRINT",EDGE,{"derivedFrom":sQuery(id+"F42.wireOp",EDGE,"E28.3.0.0")}),-1.0]])]});
            var Q6;
            Q6=makeQuery(id+"F42.imprint","IMPRINT",FACE,{"disambiguationData":[TD([[makeQuery(id+"F42.imprint","IMPRINT",EDGE,{"derivedFrom":sQuery(id+"F42.wireOp",EDGE,"E28.4.0.0")}),-1.0]])]});
            var Q7;
            Q7=makeQuery(id+"F42.imprint","IMPRINT",FACE,{"disambiguationData":[TD([[makeQuery(id+"F42.imprint","IMPRINT",EDGE,{"derivedFrom":sQuery(id+"F42.wireOp",EDGE,"E28.5.0.0")}),-1.0]])]});
            var Q8;
            Q8=makeQuery(id+"F42.imprint","IMPRINT",FACE,{"disambiguationData":[TD([[makeQuery(id+"F42.imprint","IMPRINT",EDGE,{"derivedFrom":sQuery(id+"F42.wireOp",EDGE,"E28.6.0.0")}),-1.0]])]});
            var Q9;
            Q9=makeQuery(id+"F42.imprint","IMPRINT",FACE,{"disambiguationData":[TD([[makeQuery(id+"F42.imprint","IMPRINT",EDGE,{"derivedFrom":sQuery(id+"F42.wireOp",EDGE,"E26.bottom")}),-1.0]])]});
            var Q10;
            Q10=makeQuery(id+"F42.imprint","IMPRINT",FACE,{"disambiguationData":[TD([[makeQuery(id+"F42.imprint","IMPRINT",EDGE,{"derivedFrom":sQuery(id+"F42.wireOp",EDGE,"E25.bottom")}),-1.0]])]});
            extrude(context, id + "F43", {"entities" : qUnion([Q0, Q1, Q2, Q3, Q4, Q5, Q6, Q7, Q8, Q9, Q10]), "depth" : 45 * mm, "offsetDistance" : 25 * mm});
        }
        {
            var Q0;
            Q0=qCreatedBy(makeId("Front.planeOp"),FACE);
            var sketch = newSketch(context, id + "F44", { "sketchPlane" : qUnion([Q0])});
            skLineSegment(sketch, "E29.bottom", {"start": v(-2273.83, -145.12) * mm, "end": v(-1793.83, -145.12) * mm});
            skLineSegment(sketch, "E29.top", {"start": v(-2273.83, -365.12) * mm, "end": v(-1793.83, -365.12) * mm});
            skLineSegment(sketch, "E29.left", {"start": v(-2273.83, -145.12) * mm, "end": v(-2273.83, -365.12) * mm});
            skLineSegment(sketch, "E29.right", {"start": v(-1793.83, -145.12) * mm, "end": v(-1793.83, -365.12) * mm});
            skSolve(sketch);
        }
        {
            var Q0;
            Q0 = qSketchRegion(id + "F44", true);
            extrude(context, id + "F45", {"entities" : qUnion([Q0]), "depth" : 135 * mm, "offsetDistance" : 25 * mm});
        }
        {
            var Q0;
            Q0=qCreatedBy(makeId("Front.planeOp"),FACE);
            var sketch = newSketch(context, id + "F46", { "sketchPlane" : qUnion([Q0])});
            skLineSegment(sketch, "E30.bottom", {"start": v(-2202.87, 202.24) * mm, "end": v(-1752.87, 202.24) * mm});
            skLineSegment(sketch, "E30.top", {"start": v(-2202.87, -97.76) * mm, "end": v(-1752.87, -97.76) * mm});
            skLineSegment(sketch, "E30.left", {"start": v(-2202.87, 202.24) * mm, "end": v(-2202.87, -97.76) * mm});
            skLineSegment(sketch, "E30.right", {"start": v(-1752.87, 202.24) * mm, "end": v(-1752.87, -97.76) * mm});
            skSolve(sketch);
        }
        {
            var Q0;
            Q0=makeQuery(id+"F46.imprint","IMPRINT",FACE,{"disambiguationData":[TD([[makeQuery(id+"F46.imprint","IMPRINT",EDGE,{"derivedFrom":sQuery(id+"F46.wireOp",EDGE,"E30.bottom")}),-1.0]])]});
            extrude(context, id + "F47", {"entities" : qUnion([Q0]), "depth" : 210 * mm, "offsetDistance" : 25 * mm});
        }
        {
            var Q0;
            Q0=qCreatedBy(makeId("Front.planeOp"),FACE);
            var sketch = newSketch(context, id + "F48", { "sketchPlane" : qUnion([Q0])});
            skLineSegment(sketch, "E31.bottom", {"start": v(-1736.06, -770.73) * mm, "end": v(-2216.06, -770.73) * mm});
            skLineSegment(sketch, "E31.top", {"start": v(-1736.06, -1070.73) * mm, "end": v(-2216.06, -1070.73) * mm});
            skLineSegment(sketch, "E31.left", {"start": v(-1736.06, -770.73) * mm, "end": v(-1736.06, -1070.73) * mm});
            skLineSegment(sketch, "E31.right", {"start": v(-2216.06, -770.73) * mm, "end": v(-2216.06, -1070.73) * mm});
            skSolve(sketch);
        }
        {
            var Q0;
            Q0 = qSketchRegion(id + "F48", true);
            extrude(context, id + "F49", {"entities" : qUnion([Q0]), "depth" : 110 * mm, "offsetDistance" : 25 * mm});
        }
        {
            var Q0;
            Q0=qCreatedBy(makeId("Front.planeOp"),FACE);
            var sketch = newSketch(context, id + "F50", { "sketchPlane" : qUnion([Q0])});
            skLineSegment(sketch, "E32.bottom", {"start": v(-2903.29, -733.48) * mm, "end": v(-2783.29, -733.48) * mm});
            skLineSegment(sketch, "E32.top", {"start": v(-2903.29, -1113.48) * mm, "end": v(-2783.29, -1113.48) * mm});
            skLineSegment(sketch, "E32.left", {"start": v(-2903.29, -733.48) * mm, "end": v(-2903.29, -1113.48) * mm});
            skLineSegment(sketch, "E32.right", {"start": v(-2783.29, -733.48) * mm, "end": v(-2783.29, -1113.48) * mm});
            skLineSegment(sketch, "E33.bottom", {"start": v(-2738.02, -803.81) * mm, "end": v(-2638.02, -803.81) * mm});
            skLineSegment(sketch, "E33.top", {"start": v(-2738.02, -1113.81) * mm, "end": v(-2638.02, -1113.81) * mm});
            skLineSegment(sketch, "E33.left", {"start": v(-2738.02, -803.81) * mm, "end": v(-2738.02, -1113.81) * mm});
            skLineSegment(sketch, "E33.right", {"start": v(-2638.02, -803.81) * mm, "end": v(-2638.02, -1113.81) * mm});
            skLineSegment(sketch, "E34.bottom", {"start": v(-2597.67, -870.09) * mm, "end": v(-2387.67, -870.09) * mm});
            skLineSegment(sketch, "E34.top", {"start": v(-2597.67, -1180.09) * mm, "end": v(-2387.67, -1180.09) * mm});
            skLineSegment(sketch, "E34.left", {"start": v(-2597.67, -870.09) * mm, "end": v(-2597.67, -1180.09) * mm});
            skLineSegment(sketch, "E34.right", {"start": v(-2387.67, -870.09) * mm, "end": v(-2387.67, -1180.09) * mm});
            skLineSegment(sketch, "E35.bottom", {"start": v(-2527.5, -1054.85) * mm, "end": v(-2377.5, -1054.85) * mm});
            skLineSegment(sketch, "E35.top", {"start": v(-2527.5, -1304.85) * mm, "end": v(-2377.5, -1304.85) * mm});
            skLineSegment(sketch, "E35.left", {"start": v(-2527.5, -1054.85) * mm, "end": v(-2527.5, -1304.85) * mm});
            skLineSegment(sketch, "E35.right", {"start": v(-2377.5, -1054.85) * mm, "end": v(-2377.5, -1304.85) * mm});
            skLineSegment(sketch, "E36.bottom", {"start": v(-2909.56, -1120.95) * mm, "end": v(-2609.56, -1120.95) * mm});
            skLineSegment(sketch, "E36.top", {"start": v(-2909.56, -1300.95) * mm, "end": v(-2609.56, -1300.95) * mm});
            skLineSegment(sketch, "E36.left", {"start": v(-2909.56, -1120.95) * mm, "end": v(-2909.56, -1300.95) * mm});
            skLineSegment(sketch, "E36.right", {"start": v(-2609.56, -1120.95) * mm, "end": v(-2609.56, -1300.95) * mm});
            skSolve(sketch);
        }
        {
            var Q0;
            Q0=makeQuery(id+"F50.imprint","IMPRINT",FACE,{"disambiguationData":[TD([[makeQuery(id+"F50.imprint","IMPRINT",EDGE,{"derivedFrom":sQuery(id+"F50.wireOp",EDGE,"E36.bottom")}),-1.0]])]});
            var Q1;
            Q1=makeQuery(id+"F50.imprint","IMPRINT",FACE,{"disambiguationData":[TD([[makeQuery(id+"F50.imprint","IMPRINT",EDGE,{"derivedFrom":sQuery(id+"F50.wireOp",EDGE,"E32.bottom")}),-1.0]])]});
            var Q2;
            Q2=makeQuery(id+"F50.imprint","IMPRINT",FACE,{"disambiguationData":[TD([[makeQuery(id+"F50.imprint","IMPRINT",EDGE,{"derivedFrom":sQuery(id+"F50.wireOp",EDGE,"E33.bottom")}),-1.0]])]});
            var Q3;
            {var subQ0=sQuery(id+"F50.wireOp",EDGE,"E34.right");var subQ1=sQuery(id+"F50.wireOp",EDGE,"E34.top");var subQ2=makeQuery(id+"F50.imprint","INTERSECT",VERTEX,{"derivedFrom":[subQ1,subQ0]});Q3=makeQuery(id+"F50.imprint","IMPRINT",FACE,{"disambiguationData":[TD([[makeQuery(id+"F50.imprint","IMPRINT",EDGE,{"disambiguationData":[TD([[subQ2,1.0]])],"derivedFrom":subQ1}),1.0]])]});}
            var Q4;
            {var subQ0=sQuery(id+"F50.wireOp",EDGE,"E35.top");Q4=makeQuery(id+"F50.imprint","IMPRINT",FACE,{"disambiguationData":[TD([[makeQuery(id+"F50.imprint","IMPRINT",EDGE,{"derivedFrom":subQ0}),1.0]])]});}
            extrude(context, id + "F51", {"entities" : qUnion([Q0, Q1, Q2, Q3, Q4]), "depth" : 220 * mm, "offsetDistance" : 25 * mm});
        }
        {
            var Q0;
            Q0=qCreatedBy(makeId("Front.planeOp"),FACE);
            var sketch = newSketch(context, id + "F52", { "sketchPlane" : qUnion([Q0])});
            skLineSegment(sketch, "E37.bottom", {"start": v(-2594.11, -429.4) * mm, "end": v(-2244.11, -429.4) * mm});
            skLineSegment(sketch, "E37.top", {"start": v(-2594.11, -779.4) * mm, "end": v(-2244.11, -779.4) * mm});
            skLineSegment(sketch, "E37.left", {"start": v(-2594.11, -429.4) * mm, "end": v(-2594.11, -779.4) * mm});
            skLineSegment(sketch, "E37.right", {"start": v(-2244.11, -429.4) * mm, "end": v(-2244.11, -779.4) * mm});
            skSolve(sketch);
        }
        {
            var Q0;
            Q0 = qSketchRegion(id + "F52", true);
            extrude(context, id + "F53", {"entities" : qUnion([Q0]), "depth" : 200 * mm, "offsetDistance" : 25 * mm});
        }
        {
            var Q0;
            Q0=qCreatedBy(makeId("Front.planeOp"),FACE);
            var sketch = newSketch(context, id + "F54", { "sketchPlane" : qUnion([Q0])});
            skLineSegment(sketch, "E38.bottom", {"start": v(-2804.08, 307.41) * mm, "end": v(-2304.08, 307.41) * mm});
            skLineSegment(sketch, "E38.top", {"start": v(-2804.08, -392.59) * mm, "end": v(-2304.08, -392.59) * mm});
            skLineSegment(sketch, "E38.left", {"start": v(-2804.08, 307.41) * mm, "end": v(-2804.08, -392.59) * mm});
            skLineSegment(sketch, "E38.right", {"start": v(-2304.08, 307.41) * mm, "end": v(-2304.08, -392.59) * mm});
            skSolve(sketch);
        }
        {
            var Q0;
            Q0 = qSketchRegion(id + "F54", true);
            extrude(context, id + "F55", {"entities" : qUnion([Q0]), "depth" : 200 * mm, "offsetDistance" : 25 * mm});
        }
        {
            var Q0;
            Q0=qCreatedBy(makeId("Front.planeOp"),FACE);
            var sketch = newSketch(context, id + "F56", { "sketchPlane" : qUnion([Q0])});
            skLineSegment(sketch, "E39.bottom", {"start": v(-3178.29, -446.95) * mm, "end": v(-3085.29, -446.95) * mm});
            skLineSegment(sketch, "E39.top", {"start": v(-3178.29, -561.95) * mm, "end": v(-3085.29, -561.95) * mm});
            skLineSegment(sketch, "E39.left", {"start": v(-3178.29, -446.95) * mm, "end": v(-3178.29, -561.95) * mm});
            skLineSegment(sketch, "E39.right", {"start": v(-3085.29, -446.95) * mm, "end": v(-3085.29, -561.95) * mm});
            skLineSegment(sketch, "E40.1.0.0", {"start": v(-3068.29, -446.95) * mm, "end": v(-3068.29, -561.95) * mm});
            skLineSegment(sketch, "E40.1.0.1", {"start": v(-2975.29, -446.95) * mm, "end": v(-2975.29, -561.95) * mm});
            skLineSegment(sketch, "E40.1.0.2", {"start": v(-3068.29, -446.95) * mm, "end": v(-2975.29, -446.95) * mm});
            skLineSegment(sketch, "E40.1.0.3", {"start": v(-3068.29, -561.95) * mm, "end": v(-2975.29, -561.95) * mm});
            skLineSegment(sketch, "E40.2.0.0", {"start": v(-2958.29, -446.95) * mm, "end": v(-2958.29, -561.95) * mm});
            skLineSegment(sketch, "E40.2.0.1", {"start": v(-2865.29, -446.95) * mm, "end": v(-2865.29, -561.95) * mm});
            skLineSegment(sketch, "E40.2.0.2", {"start": v(-2958.29, -446.95) * mm, "end": v(-2865.29, -446.95) * mm});
            skLineSegment(sketch, "E40.2.0.3", {"start": v(-2958.29, -561.95) * mm, "end": v(-2865.29, -561.95) * mm});
            skLineSegment(sketch, "E40.3.0.0", {"start": v(-2848.29, -446.95) * mm, "end": v(-2848.29, -561.95) * mm});
            skLineSegment(sketch, "E40.3.0.1", {"start": v(-2755.29, -446.95) * mm, "end": v(-2755.29, -561.95) * mm});
            skLineSegment(sketch, "E40.3.0.2", {"start": v(-2848.29, -446.95) * mm, "end": v(-2755.29, -446.95) * mm});
            skLineSegment(sketch, "E40.3.0.3", {"start": v(-2848.29, -561.95) * mm, "end": v(-2755.29, -561.95) * mm});
            skLineSegment(sketch, "E40.4.0.0", {"start": v(-2738.29, -446.95) * mm, "end": v(-2738.29, -561.95) * mm});
            skLineSegment(sketch, "E40.4.0.1", {"start": v(-2645.29, -446.95) * mm, "end": v(-2645.29, -561.95) * mm});
            skLineSegment(sketch, "E40.4.0.2", {"start": v(-2738.29, -446.95) * mm, "end": v(-2645.29, -446.95) * mm});
            skLineSegment(sketch, "E40.4.0.3", {"start": v(-2738.29, -561.95) * mm, "end": v(-2645.29, -561.95) * mm});
            skLineSegment(sketch, "E40.direction1", {"start": v(-3178.29, -561.95) * mm, "end": v(-3068.29, -561.95) * mm, "construction": true});
            skSolve(sketch);
        }
        {
            var Q0;
            Q0 = qSketchRegion(id + "F56", true);
            extrude(context, id + "F57", {"entities" : qUnion([Q0]), "depth" : 80 * mm, "offsetDistance" : 25 * mm});
        }
        {
            var Q0;
            Q0=qCreatedBy(makeId("Front.planeOp"),FACE);
            var sketch = newSketch(context, id + "F58", { "sketchPlane" : qUnion([Q0])});
            skLineSegment(sketch, "E41.bottom", {"start": v(-3517.45, 59.3) * mm, "end": v(-3029.45, 59.3) * mm});
            skLineSegment(sketch, "E41.top", {"start": v(-3517.45, -267.7) * mm, "end": v(-3029.45, -267.7) * mm});
            skLineSegment(sketch, "E41.left", {"start": v(-3517.45, 59.3) * mm, "end": v(-3517.45, -267.7) * mm});
            skLineSegment(sketch, "E41.right", {"start": v(-3029.45, 59.3) * mm, "end": v(-3029.45, -267.7) * mm});
            skSolve(sketch);
        }
        {
            var Q0;
            Q0 = qSketchRegion(id + "F58", true);
            extrude(context, id + "F59", {"entities" : qUnion([Q0]), "depth" : 15 * mm, "offsetDistance" : 25 * mm});
        }
        {
            var Q0;
            Q0=makeQuery(id+"F59.opExtrude","CAP_FACE",FACE,{"disambiguationData":[OSD([sQuery(id+"F58.wireOp",EDGE,"E41.bottom"),sQuery(id+"F58.wireOp",EDGE,"E41.top"),sQuery(id+"F58.wireOp",EDGE,"E41.left"),sQuery(id+"F58.wireOp",EDGE,"E41.right")])],"isStart":false});
            var sketch = newSketch(context, id + "F60", { "sketchPlane" : qUnion([Q0])});
            skLineSegment(sketch, "E42.bottom", {"start": v(-3219.18, -53) * mm, "end": v(-2975.18, -53) * mm});
            skLineSegment(sketch, "E42.top", {"start": v(-3219.18, -318) * mm, "end": v(-2975.18, -318) * mm});
            skLineSegment(sketch, "E42.left", {"start": v(-3219.18, -53) * mm, "end": v(-3219.18, -318) * mm});
            skLineSegment(sketch, "E42.right", {"start": v(-2975.18, -53) * mm, "end": v(-2975.18, -318) * mm});
            skSolve(sketch);
        }
        {
            var Q0;
            Q0 = qSketchRegion(id + "F60", true);
            extrude(context, id + "F61", {"entities" : qUnion([Q0]), "operationType" : NewBodyOperationType.ADD, "depth" : 20 * mm, "offsetDistance" : 25 * mm});
        }
        {
            var Q0;
            Q0=qCreatedBy(makeId("Front.planeOp"),FACE);
            var sketch = newSketch(context, id + "F62", { "sketchPlane" : qUnion([Q0])});
            skLineSegment(sketch, "E43.bottom", {"start": v(-3676.37, -651.46) * mm, "end": v(-3096.37, -651.46) * mm});
            skLineSegment(sketch, "E43.top", {"start": v(-3676.37, -1131.46) * mm, "end": v(-3096.37, -1131.46) * mm});
            skLineSegment(sketch, "E43.left", {"start": v(-3676.37, -651.46) * mm, "end": v(-3676.37, -1131.46) * mm});
            skLineSegment(sketch, "E43.right", {"start": v(-3096.37, -651.46) * mm, "end": v(-3096.37, -1131.46) * mm});
            skSolve(sketch);
        }
        {
            var Q0;
            Q0 = qSketchRegion(id + "F62", true);
            extrude(context, id + "F63", {"entities" : qUnion([Q0]), "depth" : 150 * mm, "offsetDistance" : 25 * mm});
        }
        {
            var Q0;
            Q0=qCreatedBy(makeId("Front.planeOp"),FACE);
            var sketch = newSketch(context, id + "F64", { "sketchPlane" : qUnion([Q0])});
            skLineSegment(sketch, "E44.bottom", {"start": v(-2169.2, -1128.26) * mm, "end": v(-1769.2, -1128.26) * mm});
            skLineSegment(sketch, "E44.top", {"start": v(-2169.2, -1278.26) * mm, "end": v(-1769.2, -1278.26) * mm});
            skLineSegment(sketch, "E44.left", {"start": v(-2169.2, -1128.26) * mm, "end": v(-2169.2, -1278.26) * mm});
            skLineSegment(sketch, "E44.right", {"start": v(-1769.2, -1128.26) * mm, "end": v(-1769.2, -1278.26) * mm});
            skSolve(sketch);
        }
        {
            var Q0;
            Q0 = qSketchRegion(id + "F64", true);
            extrude(context, id + "F65", {"entities" : qUnion([Q0]), "depth" : 120 * mm, "offsetDistance" : 25 * mm});
        }
        {
            var Q0;
            Q0=qCreatedBy(makeId("Front.planeOp"),FACE);
            var sketch = newSketch(context, id + "F66", { "sketchPlane" : qUnion([Q0])});
            skLineSegment(sketch, "E45.bottom", {"start": v(-2219.85, 817.2) * mm, "end": v(-1739.85, 817.2) * mm});
            skLineSegment(sketch, "E45.top", {"start": v(-2219.85, 237.2) * mm, "end": v(-1739.85, 237.2) * mm});
            skLineSegment(sketch, "E45.left", {"start": v(-2219.85, 817.2) * mm, "end": v(-2219.85, 237.2) * mm});
            skLineSegment(sketch, "E45.right", {"start": v(-1739.85, 817.2) * mm, "end": v(-1739.85, 237.2) * mm});
            skSolve(sketch);
        }
        {
            var Q0;
            Q0 = qSketchRegion(id + "F66", true);
            extrude(context, id + "F67", {"entities" : qUnion([Q0]), "depth" : 250 * mm, "offsetDistance" : 25 * mm});
        }
        {
            var Q0;
            Q0=qCreatedBy(makeId("Front.planeOp"),FACE);
            var sketch = newSketch(context, id + "F68", { "sketchPlane" : qUnion([Q0])});
            skLineSegment(sketch, "E46.bottom", {"start": v(-2699.87, 698.97) * mm, "end": v(-2299.87, 698.97) * mm});
            skLineSegment(sketch, "E46.top", {"start": v(-2699.87, 378.97) * mm, "end": v(-2299.87, 378.97) * mm});
            skLineSegment(sketch, "E46.left", {"start": v(-2699.87, 698.97) * mm, "end": v(-2699.87, 378.97) * mm});
            skLineSegment(sketch, "E46.right", {"start": v(-2299.87, 698.97) * mm, "end": v(-2299.87, 378.97) * mm});
            skSolve(sketch);
        }
        {
            var Q0;
            Q0 = qSketchRegion(id + "F68", true);
            extrude(context, id + "F69", {"entities" : qUnion([Q0]), "depth" : 150 * mm, "offsetDistance" : 25 * mm});
        }
        {
            var Q0;
            Q0=qCreatedBy(makeId("Front.planeOp"),FACE);
            var sketch = newSketch(context, id + "F70", { "sketchPlane" : qUnion([Q0])});
            skLineSegment(sketch, "E47.bottom", {"start": v(-3323.03, 697.53) * mm, "end": v(-2843.03, 697.53) * mm});
            skLineSegment(sketch, "E47.top", {"start": v(-3323.03, 117.53) * mm, "end": v(-2843.03, 117.53) * mm});
            skLineSegment(sketch, "E47.left", {"start": v(-3323.03, 697.53) * mm, "end": v(-3323.03, 117.53) * mm});
            skLineSegment(sketch, "E47.right", {"start": v(-2843.03, 697.53) * mm, "end": v(-2843.03, 117.53) * mm});
            skSolve(sketch);
        }
        {
            var Q0;
            Q0 = qSketchRegion(id + "F70", true);
            extrude(context, id + "F71", {"entities" : qUnion([Q0]), "depth" : 150 * mm, "offsetDistance" : 25 * mm});
        }
        {
            var Q0;
            Q0=qCreatedBy(makeId("Front.planeOp"),FACE);
            var sketch = newSketch(context, id + "F72", { "sketchPlane" : qUnion([Q0])});
            skLineSegment(sketch, "E48.bottom", {"start": v(-1701.75, 749.92) * mm, "end": v(-1431.75, 749.92) * mm});
            skLineSegment(sketch, "E48.top", {"start": v(-1701.75, 374.92) * mm, "end": v(-1431.75, 374.92) * mm});
            skLineSegment(sketch, "E48.left", {"start": v(-1701.75, 749.92) * mm, "end": v(-1701.75, 374.92) * mm});
            skLineSegment(sketch, "E48.right", {"start": v(-1431.75, 749.92) * mm, "end": v(-1431.75, 374.92) * mm});
            skSolve(sketch);
        }
        {
            var Q0;
            Q0 = qSketchRegion(id + "F72", true);
            extrude(context, id + "F73", {"entities" : qUnion([Q0]), "depth" : 10 * mm, "offsetDistance" : 25 * mm});
        }
        {
            var Q0;
            Q0=qCreatedBy(makeId("Front.planeOp"),FACE);
            var sketch = newSketch(context, id + "F74", { "sketchPlane" : qUnion([Q0])});
            skLineSegment(sketch, "E49.bottom", {"start": v(-3919.76, -144.08) * mm, "end": v(-3539.76, -144.08) * mm});
            skLineSegment(sketch, "E49.top", {"start": v(-3919.76, -624.08) * mm, "end": v(-3539.76, -624.08) * mm});
            skLineSegment(sketch, "E49.left", {"start": v(-3919.76, -144.08) * mm, "end": v(-3919.76, -624.08) * mm});
            skLineSegment(sketch, "E49.right", {"start": v(-3539.76, -144.08) * mm, "end": v(-3539.76, -624.08) * mm});
            skSolve(sketch);
        }
        {
            var Q0;
            Q0 = qSketchRegion(id + "F74", true);
            extrude(context, id + "F75", {"entities" : qUnion([Q0]), "depth" : 100 * mm, "offsetDistance" : 25 * mm});
        }
        {
            var Q0;
            Q0=qCreatedBy(makeId("Front.planeOp"),FACE);
            var sketch = newSketch(context, id + "F76", { "sketchPlane" : qUnion([Q0])});
            skLineSegment(sketch, "E50.bottom", {"start": v(-3924, 364.67) * mm, "end": v(-3544, 364.67) * mm});
            skLineSegment(sketch, "E50.top", {"start": v(-3924, -115.33) * mm, "end": v(-3544, -115.33) * mm});
            skLineSegment(sketch, "E50.left", {"start": v(-3924, 364.67) * mm, "end": v(-3924, -115.33) * mm});
            skLineSegment(sketch, "E50.right", {"start": v(-3544, 364.67) * mm, "end": v(-3544, -115.33) * mm});
            skSolve(sketch);
        }
        {
            var Q0;
            Q0 = qSketchRegion(id + "F76", true);
            extrude(context, id + "F77", {"entities" : qUnion([Q0]), "depth" : 100 * mm, "offsetDistance" : 25 * mm});
        }
        {
            var Q0;
            Q0=qCreatedBy(makeId("Front.planeOp"),FACE);
            var sketch = newSketch(context, id + "F78", { "sketchPlane" : qUnion([Q0])});
            skLineSegment(sketch, "E51.bottom", {"start": v(-3504.02, -345.49) * mm, "end": v(-3204.02, -345.49) * mm});
            skLineSegment(sketch, "E51.top", {"start": v(-3504.02, -565.49) * mm, "end": v(-3204.02, -565.49) * mm});
            skLineSegment(sketch, "E51.left", {"start": v(-3504.02, -345.49) * mm, "end": v(-3504.02, -565.49) * mm});
            skLineSegment(sketch, "E51.right", {"start": v(-3204.02, -345.49) * mm, "end": v(-3204.02, -565.49) * mm});
            skSolve(sketch);
        }
        {
            var Q0;
            Q0 = qSketchRegion(id + "F78", true);
            extrude(context, id + "F79", {"entities" : qUnion([Q0]), "depth" : 250 * mm, "offsetDistance" : 25 * mm});
        }
        {
            var Q0;
            Q0=qCreatedBy(makeId("Front.planeOp"),FACE);
            var sketch = newSketch(context, id + "F80", { "sketchPlane" : qUnion([Q0])});
            skLineSegment(sketch, "E52.bottom", {"start": v(-4183.67, -694.3) * mm, "end": v(-4023.67, -694.3) * mm});
            skLineSegment(sketch, "E52.top", {"start": v(-4183.67, -909.3) * mm, "end": v(-4023.67, -909.3) * mm});
            skLineSegment(sketch, "E52.left", {"start": v(-4183.67, -694.3) * mm, "end": v(-4183.67, -909.3) * mm});
            skLineSegment(sketch, "E52.right", {"start": v(-4023.67, -694.3) * mm, "end": v(-4023.67, -909.3) * mm});
            skSolve(sketch);
        }
        {
            var Q0;
            Q0 = qSketchRegion(id + "F80", true);
            extrude(context, id + "F81", {"entities" : qUnion([Q0]), "depth" : 15 * mm, "offsetDistance" : 25 * mm});
        }
        {
            var Q0;
            Q0=makeQuery(id+"F81.opExtrude","CAP_FACE",FACE,{"disambiguationData":[OSD([sQuery(id+"F80.wireOp",EDGE,"E52.bottom"),sQuery(id+"F80.wireOp",EDGE,"E52.top"),sQuery(id+"F80.wireOp",EDGE,"E52.left"),sQuery(id+"F80.wireOp",EDGE,"E52.right")])],"isStart":false});
            var sketch = newSketch(context, id + "F82", { "sketchPlane" : qUnion([Q0])});
            skLineSegment(sketch, "E53.bottom", {"start": v(-4065.66, -753.78) * mm, "end": v(-3925.66, -753.78) * mm});
            skLineSegment(sketch, "E53.top", {"start": v(-4065.66, -878.78) * mm, "end": v(-3925.66, -878.78) * mm});
            skLineSegment(sketch, "E53.left", {"start": v(-4065.66, -753.78) * mm, "end": v(-4065.66, -878.78) * mm});
            skLineSegment(sketch, "E53.right", {"start": v(-3925.66, -753.78) * mm, "end": v(-3925.66, -878.78) * mm});
            skSolve(sketch);
        }
        {
            var Q0;
            Q0 = qSketchRegion(id + "F82", true);
            extrude(context, id + "F83", {"entities" : qUnion([Q0]), "operationType" : NewBodyOperationType.ADD, "depth" : 11 * mm, "offsetDistance" : 25 * mm});
        }
        {
            var Q0;
            Q0=qCreatedBy(makeId("Front.planeOp"),FACE);
            var sketch = newSketch(context, id + "F84", { "sketchPlane" : qUnion([Q0])});
            skLineSegment(sketch, "E54.bottom", {"start": v(-3972.43, -913.17) * mm, "end": v(-3722.43, -913.17) * mm});
            skLineSegment(sketch, "E54.top", {"start": v(-3972.43, -1101.17) * mm, "end": v(-3722.43, -1101.17) * mm});
            skLineSegment(sketch, "E54.left", {"start": v(-3972.43, -913.17) * mm, "end": v(-3972.43, -1101.17) * mm});
            skLineSegment(sketch, "E54.right", {"start": v(-3722.43, -913.17) * mm, "end": v(-3722.43, -1101.17) * mm});
            skSolve(sketch);
        }
        {
            var Q0;
            Q0 = qSketchRegion(id + "F84", true);
            extrude(context, id + "F85", {"entities" : qUnion([Q0]), "depth" : 15 * mm, "offsetDistance" : 25 * mm});
        }
        {
            var Q0;
            Q0=qCreatedBy(makeId("Front.planeOp"),FACE);
            var sketch = newSketch(context, id + "F86", { "sketchPlane" : qUnion([Q0])});
            skLineSegment(sketch, "E55.bottom", {"start": v(-4260.56, -230.22) * mm, "end": v(-3980.56, -230.22) * mm});
            skLineSegment(sketch, "E55.top", {"start": v(-4260.56, -610.22) * mm, "end": v(-3980.56, -610.22) * mm});
            skLineSegment(sketch, "E55.left", {"start": v(-4260.56, -230.22) * mm, "end": v(-4260.56, -610.22) * mm});
            skLineSegment(sketch, "E55.right", {"start": v(-3980.56, -230.22) * mm, "end": v(-3980.56, -610.22) * mm});
            skSolve(sketch);
        }
        {
            var Q0;
            Q0 = qSketchRegion(id + "F86", true);
            extrude(context, id + "F87", {"entities" : qUnion([Q0]), "depth" : 10 * mm, "offsetDistance" : 25 * mm});
        }
        {
            var Q0;
            Q0=qCreatedBy(makeId("Front.planeOp"),FACE);
            var sketch = newSketch(context, id + "F88", { "sketchPlane" : qUnion([Q0])});
            skLineSegment(sketch, "E56.bottom", {"start": v(-4392.12, 172.67) * mm, "end": v(-3957.12, 172.67) * mm});
            skLineSegment(sketch, "E56.top", {"start": v(-4392.12, -177.33) * mm, "end": v(-3957.12, -177.33) * mm});
            skLineSegment(sketch, "E56.left", {"start": v(-4392.12, 172.67) * mm, "end": v(-4392.12, -177.33) * mm});
            skLineSegment(sketch, "E56.right", {"start": v(-3957.12, 172.67) * mm, "end": v(-3957.12, -177.33) * mm});
            skSolve(sketch);
        }
        {
            var Q0;
            Q0 = qSketchRegion(id + "F88", true);
            extrude(context, id + "F89", {"entities" : qUnion([Q0]), "depth" : 250 * mm, "offsetDistance" : 25 * mm});
        }
        {
            var Q0;
            Q0=qCreatedBy(makeId("Front.planeOp"),FACE);
            var sketch = newSketch(context, id + "F90", { "sketchPlane" : qUnion([Q0])});
            skLineSegment(sketch, "E57.bottom", {"start": v(-4440.83, 796.98) * mm, "end": v(-3980.83, 796.98) * mm});
            skLineSegment(sketch, "E57.top", {"start": v(-4440.83, 236.98) * mm, "end": v(-3980.83, 236.98) * mm});
            skLineSegment(sketch, "E57.left", {"start": v(-4440.83, 796.98) * mm, "end": v(-4440.83, 236.98) * mm});
            skLineSegment(sketch, "E57.right", {"start": v(-3980.83, 796.98) * mm, "end": v(-3980.83, 236.98) * mm});
            skSolve(sketch);
        }
        {
            var Q0;
            Q0 = qSketchRegion(id + "F90", true);
            extrude(context, id + "F91", {"entities" : qUnion([Q0]), "depth" : 100 * mm, "offsetDistance" : 25 * mm});
        }
        {
            var Q0;
            Q0=qCreatedBy(makeId("Front.planeOp"),FACE);
            var sketch = newSketch(context, id + "F92", { "sketchPlane" : qUnion([Q0])});
            skLineSegment(sketch, "E58.bottom", {"start": v(-3894.25, 712.37) * mm, "end": v(-3726.25, 712.37) * mm});
            skLineSegment(sketch, "E58.top", {"start": v(-3894.25, 483.37) * mm, "end": v(-3726.25, 483.37) * mm});
            skLineSegment(sketch, "E58.left", {"start": v(-3894.25, 712.37) * mm, "end": v(-3894.25, 483.37) * mm});
            skLineSegment(sketch, "E58.right", {"start": v(-3726.25, 712.37) * mm, "end": v(-3726.25, 483.37) * mm});
            skSolve(sketch);
        }
        {
            var Q0;
            Q0 = qSketchRegion(id + "F92", true);
            extrude(context, id + "F93", {"entities" : qUnion([Q0]), "depth" : 36 * mm, "offsetDistance" : 25 * mm});
        }
        {
            var Q0;
            Q0=qCreatedBy(makeId("Front.planeOp"),FACE);
            var sketch = newSketch(context, id + "F94", { "sketchPlane" : qUnion([Q0])});
            skLineSegment(sketch, "E59.bottom", {"start": v(-3657.49, 703.08) * mm, "end": v(-3479.49, 703.08) * mm});
            skLineSegment(sketch, "E59.top", {"start": v(-3657.49, 443.08) * mm, "end": v(-3479.49, 443.08) * mm});
            skLineSegment(sketch, "E59.left", {"start": v(-3657.49, 703.08) * mm, "end": v(-3657.49, 443.08) * mm});
            skLineSegment(sketch, "E59.right", {"start": v(-3479.49, 703.08) * mm, "end": v(-3479.49, 443.08) * mm});
            skSolve(sketch);
        }
        {
            var Q0;
            Q0 = qSketchRegion(id + "F94", true);
            extrude(context, id + "F95", {"entities" : qUnion([Q0]), "depth" : 10 * mm, "offsetDistance" : 25 * mm});
        }
        {
            var Q0;
            Q0=qCreatedBy(makeId("Front.planeOp"),FACE);
            var sketch = newSketch(context, id + "F96", { "sketchPlane" : qUnion([Q0])});
            skLineSegment(sketch, "E60.bottom", {"start": v(-4877.93, 636.75) * mm, "end": v(-4627.93, 636.75) * mm});
            skLineSegment(sketch, "E60.top", {"start": v(-4877.93, 441.75) * mm, "end": v(-4627.93, 441.75) * mm});
            skLineSegment(sketch, "E60.left", {"start": v(-4877.93, 636.75) * mm, "end": v(-4877.93, 441.75) * mm});
            skLineSegment(sketch, "E60.right", {"start": v(-4627.93, 636.75) * mm, "end": v(-4627.93, 441.75) * mm});
            skSolve(sketch);
        }
        {
            var Q0;
            Q0 = qSketchRegion(id + "F96", true);
            extrude(context, id + "F97", {"entities" : qUnion([Q0]), "depth" : 10 * mm, "offsetDistance" : 25 * mm});
        }
        {
            var Q0;
            Q0=qCreatedBy(makeId("Front.planeOp"),FACE);
            var sketch = newSketch(context, id + "F98", { "sketchPlane" : qUnion([Q0])});
            skLineSegment(sketch, "E61.bottom", {"start": v(-4880.54, 417.79) * mm, "end": v(-4630.54, 417.79) * mm});
            skLineSegment(sketch, "E61.top", {"start": v(-4880.54, 222.79) * mm, "end": v(-4630.54, 222.79) * mm});
            skLineSegment(sketch, "E61.left", {"start": v(-4880.54, 417.79) * mm, "end": v(-4880.54, 222.79) * mm});
            skLineSegment(sketch, "E61.right", {"start": v(-4630.54, 417.79) * mm, "end": v(-4630.54, 222.79) * mm});
            skSolve(sketch);
        }
        {
            var Q0;
            Q0 = qSketchRegion(id + "F98", true);
            extrude(context, id + "F99", {"entities" : qUnion([Q0]), "depth" : 10 * mm, "offsetDistance" : 25 * mm});
        }
        {
            var Q0;
            Q0=qCreatedBy(makeId("Front.planeOp"),FACE);
            var sketch = newSketch(context, id + "F100", { "sketchPlane" : qUnion([Q0])});
            skLineSegment(sketch, "E62.bottom", {"start": v(-5209.22, 652.57) * mm, "end": v(-4959.22, 652.57) * mm});
            skLineSegment(sketch, "E62.top", {"start": v(-5209.22, 457.57) * mm, "end": v(-4959.22, 457.57) * mm});
            skLineSegment(sketch, "E62.left", {"start": v(-5209.22, 652.57) * mm, "end": v(-5209.22, 457.57) * mm});
            skLineSegment(sketch, "E62.right", {"start": v(-4959.22, 652.57) * mm, "end": v(-4959.22, 457.57) * mm});
            skSolve(sketch);
        }
        {
            var Q0;
            Q0 = qSketchRegion(id + "F100", true);
            extrude(context, id + "F101", {"entities" : qUnion([Q0]), "depth" : 10 * mm, "offsetDistance" : 25 * mm});
        }
        {
            var Q0;
            Q0=qCreatedBy(makeId("Front.planeOp"),FACE);
            var sketch = newSketch(context, id + "F102", { "sketchPlane" : qUnion([Q0])});
            skLineSegment(sketch, "E63.bottom", {"start": v(-5198.92, 428.04) * mm, "end": v(-4948.92, 428.04) * mm});
            skLineSegment(sketch, "E63.top", {"start": v(-5198.92, 233.04) * mm, "end": v(-4948.92, 233.04) * mm});
            skLineSegment(sketch, "E63.left", {"start": v(-5198.92, 428.04) * mm, "end": v(-5198.92, 233.04) * mm});
            skLineSegment(sketch, "E63.right", {"start": v(-4948.92, 428.04) * mm, "end": v(-4948.92, 233.04) * mm});
            skSolve(sketch);
        }
        {
            var Q0;
            Q0 = qSketchRegion(id + "F102", true);
            extrude(context, id + "F103", {"entities" : qUnion([Q0]), "depth" : 10 * mm, "offsetDistance" : 25 * mm});
        }
        {
            var Q0;
            Q0=qCreatedBy(makeId("Front.planeOp"),FACE);
            var sketch = newSketch(context, id + "F104", { "sketchPlane" : qUnion([Q0])});
            skLineSegment(sketch, "E64.bottom", {"start": v(-4477.46, 114.3) * mm, "end": v(-4452.46, 114.3) * mm});
            skLineSegment(sketch, "E64.top", {"start": v(-4477.46, 39.3) * mm, "end": v(-4452.46, 39.3) * mm});
            skLineSegment(sketch, "E64.left", {"start": v(-4477.46, 114.3) * mm, "end": v(-4477.46, 39.3) * mm});
            skLineSegment(sketch, "E64.right", {"start": v(-4452.46, 114.3) * mm, "end": v(-4452.46, 39.3) * mm});
            skSolve(sketch);
        }
        {
            var Q0;
            Q0 = qSketchRegion(id + "F104", true);
            extrude(context, id + "F105", {"entities" : qUnion([Q0]), "depth" : 25 * mm, "offsetDistance" : 25 * mm});
        }
        {
            var Q0;
            Q0=qCreatedBy(makeId("Front.planeOp"),FACE);
            var sketch = newSketch(context, id + "F106", { "sketchPlane" : qUnion([Q0])});
            skLineSegment(sketch, "E65.bottom", {"start": v(-4869.58, 99.4) * mm, "end": v(-4569.58, 99.4) * mm});
            skLineSegment(sketch, "E65.top", {"start": v(-4869.58, -160.6) * mm, "end": v(-4569.58, -160.6) * mm});
            skLineSegment(sketch, "E65.left", {"start": v(-4869.58, 99.4) * mm, "end": v(-4869.58, -160.6) * mm});
            skLineSegment(sketch, "E65.right", {"start": v(-4569.58, 99.4) * mm, "end": v(-4569.58, -160.6) * mm});
            skSolve(sketch);
        }
        {
            var Q0;
            Q0 = qSketchRegion(id + "F106", true);
            extrude(context, id + "F107", {"entities" : qUnion([Q0]), "depth" : 250 * mm, "offsetDistance" : 25 * mm});
        }
        {
            var Q0;
            Q0=qCreatedBy(makeId("Front.planeOp"),FACE);
            var sketch = newSketch(context, id + "F108", { "sketchPlane" : qUnion([Q0])});
            skLineSegment(sketch, "E66.bottom", {"start": v(-4614.13, -266.22) * mm, "end": v(-4364.13, -266.22) * mm});
            skLineSegment(sketch, "E66.top", {"start": v(-4614.13, -516.22) * mm, "end": v(-4364.13, -516.22) * mm});
            skLineSegment(sketch, "E66.left", {"start": v(-4614.13, -266.22) * mm, "end": v(-4614.13, -516.22) * mm});
            skLineSegment(sketch, "E66.right", {"start": v(-4364.13, -266.22) * mm, "end": v(-4364.13, -516.22) * mm});
            skSolve(sketch);
        }
        {
            var Q0;
            Q0 = qSketchRegion(id + "F108", true);
            extrude(context, id + "F109", {"entities" : qUnion([Q0]), "depth" : 10 * mm, "offsetDistance" : 25 * mm});
        }
        {
            var Q0;
            Q0=qCreatedBy(makeId("Front.planeOp"),FACE);
            var sketch = newSketch(context, id + "F110", { "sketchPlane" : qUnion([Q0])});
            skLineSegment(sketch, "E67.bottom", {"start": v(-4943.4, -270.47) * mm, "end": v(-4643.4, -270.47) * mm});
            skLineSegment(sketch, "E67.top", {"start": v(-4943.4, -510.47) * mm, "end": v(-4643.4, -510.47) * mm});
            skLineSegment(sketch, "E67.left", {"start": v(-4943.4, -270.47) * mm, "end": v(-4943.4, -510.47) * mm});
            skLineSegment(sketch, "E67.right", {"start": v(-4643.4, -270.47) * mm, "end": v(-4643.4, -510.47) * mm});
            skSolve(sketch);
        }
        {
            var Q0;
            Q0 = qSketchRegion(id + "F110", true);
            extrude(context, id + "F111", {"entities" : qUnion([Q0]), "depth" : 10 * mm, "offsetDistance" : 25 * mm});
        }
        {
            var Q0;
            Q0=qCreatedBy(makeId("Front.planeOp"),FACE);
            var sketch = newSketch(context, id + "F112", { "sketchPlane" : qUnion([Q0])});
            skLineSegment(sketch, "E68.bottom", {"start": v(-4823.96, -538.62) * mm, "end": v(-4348.96, -538.62) * mm});
            skLineSegment(sketch, "E68.top", {"start": v(-4823.96, -903.62) * mm, "end": v(-4348.96, -903.62) * mm});
            skLineSegment(sketch, "E68.left", {"start": v(-4823.96, -538.62) * mm, "end": v(-4823.96, -903.62) * mm});
            skLineSegment(sketch, "E68.right", {"start": v(-4348.96, -538.62) * mm, "end": v(-4348.96, -903.62) * mm});
            skSolve(sketch);
        }
        {
            var Q0;
            Q0 = qSketchRegion(id + "F112", true);
            extrude(context, id + "F113", {"entities" : qUnion([Q0]), "depth" : 200 * mm, "offsetDistance" : 25 * mm});
        }
        {
            var Q0;
            Q0=qCreatedBy(makeId("Front.planeOp"),FACE);
            var sketch = newSketch(context, id + "F114", { "sketchPlane" : qUnion([Q0])});
            skLineSegment(sketch, "E69.bottom", {"start": v(-4223.02, -951.45) * mm, "end": v(-4008.02, -951.45) * mm});
            skLineSegment(sketch, "E69.top", {"start": v(-4223.02, -1191.45) * mm, "end": v(-4008.02, -1191.45) * mm});
            skLineSegment(sketch, "E69.left", {"start": v(-4223.02, -951.45) * mm, "end": v(-4223.02, -1191.45) * mm});
            skLineSegment(sketch, "E69.right", {"start": v(-4008.02, -951.45) * mm, "end": v(-4008.02, -1191.45) * mm});
            skSolve(sketch);
        }
        {
            var Q0;
            Q0 = qSketchRegion(id + "F114", true);
            extrude(context, id + "F115", {"entities" : qUnion([Q0]), "depth" : 25 * mm, "offsetDistance" : 25 * mm});
        }
        {
            var Q0;
            Q0=qCreatedBy(makeId("Front.planeOp"),FACE);
            var sketch = newSketch(context, id + "F116", { "sketchPlane" : qUnion([Q0])});
            skLineSegment(sketch, "E70.bottom", {"start": v(-4754.17, -945.13) * mm, "end": v(-4274.17, -945.13) * mm});
            skLineSegment(sketch, "E70.top", {"start": v(-4754.17, -1325.13) * mm, "end": v(-4274.17, -1325.13) * mm});
            skLineSegment(sketch, "E70.left", {"start": v(-4754.17, -945.13) * mm, "end": v(-4754.17, -1325.13) * mm});
            skLineSegment(sketch, "E70.right", {"start": v(-4274.17, -945.13) * mm, "end": v(-4274.17, -1325.13) * mm});
            skSolve(sketch);
        }
        {
            var Q0;
            Q0 = qSketchRegion(id + "F116", true);
            extrude(context, id + "F117", {"entities" : qUnion([Q0]), "depth" : 150 * mm, "offsetDistance" : 25 * mm});
        }
        {
            var Q0;
            Q0=qCreatedBy(makeId("Front.planeOp"),FACE);
            var sketch = newSketch(context, id + "F118", { "sketchPlane" : qUnion([Q0])});
            skLineSegment(sketch, "E71.bottom", {"start": v(-5287.7, -937.46) * mm, "end": v(-4807.7, -937.46) * mm});
            skLineSegment(sketch, "E71.top", {"start": v(-5287.7, -1317.46) * mm, "end": v(-4807.7, -1317.46) * mm});
            skLineSegment(sketch, "E71.left", {"start": v(-5287.7, -937.46) * mm, "end": v(-5287.7, -1317.46) * mm});
            skLineSegment(sketch, "E71.right", {"start": v(-4807.7, -937.46) * mm, "end": v(-4807.7, -1317.46) * mm});
            skSolve(sketch);
        }
        {
            var Q0;
            Q0 = qSketchRegion(id + "F118", true);
            extrude(context, id + "F119", {"entities" : qUnion([Q0]), "depth" : 150 * mm, "offsetDistance" : 25 * mm});
        }
        {
            var Q0;
            Q0=qCreatedBy(makeId("Front.planeOp"),FACE);
            var sketch = newSketch(context, id + "F120", { "sketchPlane" : qUnion([Q0])});
            skLineSegment(sketch, "E72.bottom", {"start": v(-5443.22, -326.78) * mm, "end": v(-4963.22, -326.78) * mm});
            skLineSegment(sketch, "E72.top", {"start": v(-5443.22, -906.78) * mm, "end": v(-4963.22, -906.78) * mm});
            skLineSegment(sketch, "E72.left", {"start": v(-5443.22, -326.78) * mm, "end": v(-5443.22, -906.78) * mm});
            skLineSegment(sketch, "E72.right", {"start": v(-4963.22, -326.78) * mm, "end": v(-4963.22, -906.78) * mm});
            skSolve(sketch);
        }
        {
            var Q0;
            Q0 = qSketchRegion(id + "F120", true);
            extrude(context, id + "F121", {"entities" : qUnion([Q0]), "depth" : 70 * mm, "offsetDistance" : 25 * mm});
        }
        {
            var Q0;
            Q0=qCreatedBy(makeId("Front.planeOp"),FACE);
            var sketch = newSketch(context, id + "F122", { "sketchPlane" : qUnion([Q0])});
            skLineSegment(sketch, "E73.bottom", {"start": v(-5499.36, 141.22) * mm, "end": v(-5339.36, 141.22) * mm});
            skLineSegment(sketch, "E73.top", {"start": v(-5499.36, -208.78) * mm, "end": v(-5339.36, -208.78) * mm});
            skLineSegment(sketch, "E73.left", {"start": v(-5499.36, 141.22) * mm, "end": v(-5499.36, -208.78) * mm});
            skLineSegment(sketch, "E73.right", {"start": v(-5339.36, 141.22) * mm, "end": v(-5339.36, -208.78) * mm});
            skLineSegment(sketch, "E74.1.0.0", {"start": v(-5149.36, 141.22) * mm, "end": v(-5149.36, -208.78) * mm});
            skLineSegment(sketch, "E74.1.0.1", {"start": v(-5309.36, -208.78) * mm, "end": v(-5149.36, -208.78) * mm});
            skLineSegment(sketch, "E74.1.0.2", {"start": v(-5309.36, 141.22) * mm, "end": v(-5149.36, 141.22) * mm});
            skLineSegment(sketch, "E74.1.0.3", {"start": v(-5309.36, 141.22) * mm, "end": v(-5309.36, -208.78) * mm});
            skLineSegment(sketch, "E74.2.0.0", {"start": v(-4959.36, 141.22) * mm, "end": v(-4959.36, -208.78) * mm});
            skLineSegment(sketch, "E74.2.0.1", {"start": v(-5119.36, -208.78) * mm, "end": v(-4959.36, -208.78) * mm});
            skLineSegment(sketch, "E74.2.0.2", {"start": v(-5119.36, 141.22) * mm, "end": v(-4959.36, 141.22) * mm});
            skLineSegment(sketch, "E74.2.0.3", {"start": v(-5119.36, 141.22) * mm, "end": v(-5119.36, -208.78) * mm});
            skLineSegment(sketch, "E74.direction1", {"start": v(-5499.36, -208.78) * mm, "end": v(-5309.36, -208.78) * mm, "construction": true});
            skSolve(sketch);
        }
        {
            var Q0;
            Q0 = qSketchRegion(id + "F122", true);
            extrude(context, id + "F123", {"entities" : qUnion([Q0]), "depth" : 150 * mm, "offsetDistance" : 25 * mm});
        }
        {
            var Q0;
            Q0=qCreatedBy(makeId("Front.planeOp"),FACE);
            var sketch = newSketch(context, id + "F124", { "sketchPlane" : qUnion([Q0])});
            skLineSegment(sketch, "E75.bottom", {"start": v(-5782.95, -252.72) * mm, "end": v(-5482.95, -252.72) * mm});
            skLineSegment(sketch, "E75.top", {"start": v(-5782.95, -552.72) * mm, "end": v(-5482.95, -552.72) * mm});
            skLineSegment(sketch, "E75.left", {"start": v(-5782.95, -252.72) * mm, "end": v(-5782.95, -552.72) * mm});
            skLineSegment(sketch, "E75.right", {"start": v(-5482.95, -252.72) * mm, "end": v(-5482.95, -552.72) * mm});
            skSolve(sketch);
        }
        {
            var Q0;
            Q0 = qSketchRegion(id + "F124", true);
            extrude(context, id + "F125", {"entities" : qUnion([Q0]), "depth" : 230 * mm, "offsetDistance" : 25 * mm});
        }
        {
            var Q0;
            Q0=qCreatedBy(makeId("Front.planeOp"),FACE);
            var sketch = newSketch(context, id + "F126", { "sketchPlane" : qUnion([Q0])});
            skLineSegment(sketch, "E76.bottom", {"start": v(-6126.54, -742.24) * mm, "end": v(-5986.54, -742.24) * mm});
            skLineSegment(sketch, "E76.top", {"start": v(-6126.54, -862.24) * mm, "end": v(-5986.54, -862.24) * mm});
            skLineSegment(sketch, "E76.left", {"start": v(-6126.54, -742.24) * mm, "end": v(-6126.54, -862.24) * mm});
            skLineSegment(sketch, "E76.right", {"start": v(-5986.54, -742.24) * mm, "end": v(-5986.54, -862.24) * mm});
            skLineSegment(sketch, "E77.0.1.0", {"start": v(-6126.54, -722.24) * mm, "end": v(-5986.54, -722.24) * mm});
            skLineSegment(sketch, "E77.0.1.1", {"start": v(-6126.54, -602.24) * mm, "end": v(-5986.54, -602.24) * mm});
            skLineSegment(sketch, "E77.0.1.2", {"start": v(-5986.54, -602.24) * mm, "end": v(-5986.54, -722.24) * mm});
            skLineSegment(sketch, "E77.0.1.3", {"start": v(-6126.54, -602.24) * mm, "end": v(-6126.54, -722.24) * mm});
            skLineSegment(sketch, "E77.1.0.0", {"start": v(-5966.54, -862.24) * mm, "end": v(-5826.54, -862.24) * mm});
            skLineSegment(sketch, "E77.1.0.1", {"start": v(-5966.54, -742.24) * mm, "end": v(-5826.54, -742.24) * mm});
            skLineSegment(sketch, "E77.1.0.2", {"start": v(-5826.54, -742.24) * mm, "end": v(-5826.54, -862.24) * mm});
            skLineSegment(sketch, "E77.1.0.3", {"start": v(-5966.54, -742.24) * mm, "end": v(-5966.54, -862.24) * mm});
            skLineSegment(sketch, "E77.1.1.0", {"start": v(-5966.54, -722.24) * mm, "end": v(-5826.54, -722.24) * mm});
            skLineSegment(sketch, "E77.1.1.1", {"start": v(-5966.54, -602.24) * mm, "end": v(-5826.54, -602.24) * mm});
            skLineSegment(sketch, "E77.1.1.2", {"start": v(-5826.54, -602.24) * mm, "end": v(-5826.54, -722.24) * mm});
            skLineSegment(sketch, "E77.1.1.3", {"start": v(-5966.54, -602.24) * mm, "end": v(-5966.54, -722.24) * mm});
            skLineSegment(sketch, "E77.2.0.0", {"start": v(-5806.54, -862.24) * mm, "end": v(-5666.54, -862.24) * mm});
            skLineSegment(sketch, "E77.2.0.1", {"start": v(-5806.54, -742.24) * mm, "end": v(-5666.54, -742.24) * mm});
            skLineSegment(sketch, "E77.2.0.2", {"start": v(-5666.54, -742.24) * mm, "end": v(-5666.54, -862.24) * mm});
            skLineSegment(sketch, "E77.2.0.3", {"start": v(-5806.54, -742.24) * mm, "end": v(-5806.54, -862.24) * mm});
            skLineSegment(sketch, "E77.2.1.0", {"start": v(-5806.54, -722.24) * mm, "end": v(-5666.54, -722.24) * mm});
            skLineSegment(sketch, "E77.2.1.1", {"start": v(-5806.54, -602.24) * mm, "end": v(-5666.54, -602.24) * mm});
            skLineSegment(sketch, "E77.2.1.2", {"start": v(-5666.54, -602.24) * mm, "end": v(-5666.54, -722.24) * mm});
            skLineSegment(sketch, "E77.2.1.3", {"start": v(-5806.54, -602.24) * mm, "end": v(-5806.54, -722.24) * mm});
            skLineSegment(sketch, "E77.3.0.0", {"start": v(-5646.54, -862.24) * mm, "end": v(-5506.54, -862.24) * mm});
            skLineSegment(sketch, "E77.3.0.1", {"start": v(-5646.54, -742.24) * mm, "end": v(-5506.54, -742.24) * mm});
            skLineSegment(sketch, "E77.3.0.2", {"start": v(-5506.54, -742.24) * mm, "end": v(-5506.54, -862.24) * mm});
            skLineSegment(sketch, "E77.3.0.3", {"start": v(-5646.54, -742.24) * mm, "end": v(-5646.54, -862.24) * mm});
            skLineSegment(sketch, "E77.3.1.0", {"start": v(-5646.54, -722.24) * mm, "end": v(-5506.54, -722.24) * mm});
            skLineSegment(sketch, "E77.3.1.1", {"start": v(-5646.54, -602.24) * mm, "end": v(-5506.54, -602.24) * mm});
            skLineSegment(sketch, "E77.3.1.2", {"start": v(-5506.54, -602.24) * mm, "end": v(-5506.54, -722.24) * mm});
            skLineSegment(sketch, "E77.3.1.3", {"start": v(-5646.54, -602.24) * mm, "end": v(-5646.54, -722.24) * mm});
            skLineSegment(sketch, "E77.direction1", {"start": v(-6126.54, -862.24) * mm, "end": v(-5966.54, -862.24) * mm, "construction": true});
            skLineSegment(sketch, "E77.direction2", {"start": v(-6126.54, -862.24) * mm, "end": v(-6126.54, -722.24) * mm, "construction": true});
            skSolve(sketch);
        }
        {
            var Q0;
            Q0 = qSketchRegion(id + "F126", true);
            extrude(context, id + "F127", {"entities" : qUnion([Q0]), "depth" : 50 * mm, "offsetDistance" : 25 * mm});
        }
        {
            var Q0;
            Q0=qCreatedBy(makeId("Front.planeOp"),FACE);
            var sketch = newSketch(context, id + "F128", { "sketchPlane" : qUnion([Q0])});
            skLineSegment(sketch, "E78.bottom", {"start": v(-5766.23, -1447.09) * mm, "end": v(-5636.23, -1447.09) * mm});
            skLineSegment(sketch, "E78.top", {"start": v(-5766.23, -1587.09) * mm, "end": v(-5636.23, -1587.09) * mm});
            skLineSegment(sketch, "E78.left", {"start": v(-5766.23, -1447.09) * mm, "end": v(-5766.23, -1587.09) * mm});
            skLineSegment(sketch, "E78.right", {"start": v(-5636.23, -1447.09) * mm, "end": v(-5636.23, -1587.09) * mm});
            skLineSegment(sketch, "E79.0.1.0", {"start": v(-5636.23, -1287.09) * mm, "end": v(-5636.23, -1427.09) * mm});
            skLineSegment(sketch, "E79.0.1.1", {"start": v(-5766.23, -1427.09) * mm, "end": v(-5636.23, -1427.09) * mm});
            skLineSegment(sketch, "E79.0.1.2", {"start": v(-5766.23, -1287.09) * mm, "end": v(-5766.23, -1427.09) * mm});
            skLineSegment(sketch, "E79.0.1.3", {"start": v(-5766.23, -1287.09) * mm, "end": v(-5636.23, -1287.09) * mm});
            skLineSegment(sketch, "E79.0.2.0", {"start": v(-5636.23, -1127.09) * mm, "end": v(-5636.23, -1267.09) * mm});
            skLineSegment(sketch, "E79.0.2.1", {"start": v(-5766.23, -1267.09) * mm, "end": v(-5636.23, -1267.09) * mm});
            skLineSegment(sketch, "E79.0.2.2", {"start": v(-5766.23, -1127.09) * mm, "end": v(-5766.23, -1267.09) * mm});
            skLineSegment(sketch, "E79.0.2.3", {"start": v(-5766.23, -1127.09) * mm, "end": v(-5636.23, -1127.09) * mm});
            skLineSegment(sketch, "E79.0.3.0", {"start": v(-5636.23, -967.09) * mm, "end": v(-5636.23, -1107.09) * mm});
            skLineSegment(sketch, "E79.0.3.1", {"start": v(-5766.23, -1107.09) * mm, "end": v(-5636.23, -1107.09) * mm});
            skLineSegment(sketch, "E79.0.3.2", {"start": v(-5766.23, -967.09) * mm, "end": v(-5766.23, -1107.09) * mm});
            skLineSegment(sketch, "E79.0.3.3", {"start": v(-5766.23, -967.09) * mm, "end": v(-5636.23, -967.09) * mm});
            skLineSegment(sketch, "E79.1.0.0", {"start": v(-5486.23, -1447.09) * mm, "end": v(-5486.23, -1587.09) * mm});
            skLineSegment(sketch, "E79.1.0.1", {"start": v(-5616.23, -1587.09) * mm, "end": v(-5486.23, -1587.09) * mm});
            skLineSegment(sketch, "E79.1.0.2", {"start": v(-5616.23, -1447.09) * mm, "end": v(-5616.23, -1587.09) * mm});
            skLineSegment(sketch, "E79.1.0.3", {"start": v(-5616.23, -1447.09) * mm, "end": v(-5486.23, -1447.09) * mm});
            skLineSegment(sketch, "E79.1.1.0", {"start": v(-5486.23, -1287.09) * mm, "end": v(-5486.23, -1427.09) * mm});
            skLineSegment(sketch, "E79.1.1.1", {"start": v(-5616.23, -1427.09) * mm, "end": v(-5486.23, -1427.09) * mm});
            skLineSegment(sketch, "E79.1.1.2", {"start": v(-5616.23, -1287.09) * mm, "end": v(-5616.23, -1427.09) * mm});
            skLineSegment(sketch, "E79.1.1.3", {"start": v(-5616.23, -1287.09) * mm, "end": v(-5486.23, -1287.09) * mm});
            skLineSegment(sketch, "E79.1.2.0", {"start": v(-5486.23, -1127.09) * mm, "end": v(-5486.23, -1267.09) * mm});
            skLineSegment(sketch, "E79.1.2.1", {"start": v(-5616.23, -1267.09) * mm, "end": v(-5486.23, -1267.09) * mm});
            skLineSegment(sketch, "E79.1.2.2", {"start": v(-5616.23, -1127.09) * mm, "end": v(-5616.23, -1267.09) * mm});
            skLineSegment(sketch, "E79.1.2.3", {"start": v(-5616.23, -1127.09) * mm, "end": v(-5486.23, -1127.09) * mm});
            skLineSegment(sketch, "E79.1.3.0", {"start": v(-5486.23, -967.09) * mm, "end": v(-5486.23, -1107.09) * mm});
            skLineSegment(sketch, "E79.1.3.1", {"start": v(-5616.23, -1107.09) * mm, "end": v(-5486.23, -1107.09) * mm});
            skLineSegment(sketch, "E79.1.3.2", {"start": v(-5616.23, -967.09) * mm, "end": v(-5616.23, -1107.09) * mm});
            skLineSegment(sketch, "E79.1.3.3", {"start": v(-5616.23, -967.09) * mm, "end": v(-5486.23, -967.09) * mm});
            skLineSegment(sketch, "E79.2.0.0", {"start": v(-5336.23, -1447.09) * mm, "end": v(-5336.23, -1587.09) * mm});
            skLineSegment(sketch, "E79.2.0.1", {"start": v(-5466.23, -1587.09) * mm, "end": v(-5336.23, -1587.09) * mm});
            skLineSegment(sketch, "E79.2.0.2", {"start": v(-5466.23, -1447.09) * mm, "end": v(-5466.23, -1587.09) * mm});
            skLineSegment(sketch, "E79.2.0.3", {"start": v(-5466.23, -1447.09) * mm, "end": v(-5336.23, -1447.09) * mm});
            skLineSegment(sketch, "E79.2.1.0", {"start": v(-5336.23, -1287.09) * mm, "end": v(-5336.23, -1427.09) * mm});
            skLineSegment(sketch, "E79.2.1.1", {"start": v(-5466.23, -1427.09) * mm, "end": v(-5336.23, -1427.09) * mm});
            skLineSegment(sketch, "E79.2.1.2", {"start": v(-5466.23, -1287.09) * mm, "end": v(-5466.23, -1427.09) * mm});
            skLineSegment(sketch, "E79.2.1.3", {"start": v(-5466.23, -1287.09) * mm, "end": v(-5336.23, -1287.09) * mm});
            skLineSegment(sketch, "E79.2.2.0", {"start": v(-5336.23, -1127.09) * mm, "end": v(-5336.23, -1267.09) * mm});
            skLineSegment(sketch, "E79.2.2.1", {"start": v(-5466.23, -1267.09) * mm, "end": v(-5336.23, -1267.09) * mm});
            skLineSegment(sketch, "E79.2.2.2", {"start": v(-5466.23, -1127.09) * mm, "end": v(-5466.23, -1267.09) * mm});
            skLineSegment(sketch, "E79.2.2.3", {"start": v(-5466.23, -1127.09) * mm, "end": v(-5336.23, -1127.09) * mm});
            skLineSegment(sketch, "E79.2.3.0", {"start": v(-5336.23, -967.09) * mm, "end": v(-5336.23, -1107.09) * mm});
            skLineSegment(sketch, "E79.2.3.1", {"start": v(-5466.23, -1107.09) * mm, "end": v(-5336.23, -1107.09) * mm});
            skLineSegment(sketch, "E79.2.3.2", {"start": v(-5466.23, -967.09) * mm, "end": v(-5466.23, -1107.09) * mm});
            skLineSegment(sketch, "E79.2.3.3", {"start": v(-5466.23, -967.09) * mm, "end": v(-5336.23, -967.09) * mm});
            skLineSegment(sketch, "E79.direction1", {"start": v(-5766.23, -1587.09) * mm, "end": v(-5616.23, -1587.09) * mm, "construction": true});
            skLineSegment(sketch, "E79.direction2", {"start": v(-5766.23, -1587.09) * mm, "end": v(-5766.23, -1427.09) * mm, "construction": true});
            skSolve(sketch);
        }
        {
            var Q0;
            Q0 = qSketchRegion(id + "F128", true);
            extrude(context, id + "F129", {"entities" : qUnion([Q0]), "depth" : 115 * mm, "offsetDistance" : 25 * mm});
        }
        {
            var Q0;
            Q0=qCreatedBy(makeId("Front.planeOp"),FACE);
            var sketch = newSketch(context, id + "F130", { "sketchPlane" : qUnion([Q0])});
            skLineSegment(sketch, "E80.bottom", {"start": v(-6093.34, -953.3) * mm, "end": v(-5828.34, -953.3) * mm});
            skLineSegment(sketch, "E80.top", {"start": v(-6093.34, -1108.3) * mm, "end": v(-5828.34, -1108.3) * mm});
            skLineSegment(sketch, "E80.left", {"start": v(-6093.34, -953.3) * mm, "end": v(-6093.34, -1108.3) * mm});
            skLineSegment(sketch, "E80.right", {"start": v(-5828.34, -953.3) * mm, "end": v(-5828.34, -1108.3) * mm});
            skSolve(sketch);
        }
        {
            var Q0;
            Q0 = qSketchRegion(id + "F130", true);
            extrude(context, id + "F131", {"entities" : qUnion([Q0]), "depth" : 130 * mm, "offsetDistance" : 25 * mm});
        }
        {
            var Q0;
            Q0=qCreatedBy(makeId("Front.planeOp"),FACE);
            var sketch = newSketch(context, id + "F132", { "sketchPlane" : qUnion([Q0])});
            skLineSegment(sketch, "E81.bottom", {"start": v(397.32, 794.54) * mm, "end": v(637.32, 794.54) * mm});
            skLineSegment(sketch, "E81.top", {"start": v(397.32, 554.54) * mm, "end": v(637.32, 554.54) * mm});
            skLineSegment(sketch, "E81.left", {"start": v(397.32, 794.54) * mm, "end": v(397.32, 554.54) * mm});
            skLineSegment(sketch, "E81.right", {"start": v(637.32, 794.54) * mm, "end": v(637.32, 554.54) * mm});
            skSolve(sketch);
        }
        {
            var Q0;
            Q0 = qSketchRegion(id + "F132", true);
            extrude(context, id + "F133", {"entities" : qUnion([Q0]), "depth" : 50 * mm, "offsetDistance" : 25 * mm});
        }
        {
            var Q0;
            Q0=qCreatedBy(makeId("Front.planeOp"),FACE);
            var sketch = newSketch(context, id + "F134", { "sketchPlane" : qUnion([Q0])});
            skLineSegment(sketch, "E82.bottom", {"start": v(745.11, 769.84) * mm, "end": v(1060.11, 769.84) * mm});
            skLineSegment(sketch, "E82.top", {"start": v(745.11, 454.84) * mm, "end": v(1060.11, 454.84) * mm});
            skLineSegment(sketch, "E82.left", {"start": v(745.11, 769.84) * mm, "end": v(745.11, 454.84) * mm});
            skLineSegment(sketch, "E82.right", {"start": v(1060.11, 769.84) * mm, "end": v(1060.11, 454.84) * mm});
            skSolve(sketch);
        }
        {
            var Q0;
            Q0 = qSketchRegion(id + "F134", true);
            extrude(context, id + "F135", {"entities" : qUnion([Q0]), "depth" : 10 * mm, "offsetDistance" : 25 * mm});
        }
        {
            var Q0;
            Q0=qCreatedBy(makeId("Front.planeOp"),FACE);
            var sketch = newSketch(context, id + "F136", { "sketchPlane" : qUnion([Q0])});
            skLineSegment(sketch, "E83.bottom", {"start": v(1026.4, 293.38) * mm, "end": v(1341.4, 293.38) * mm});
            skLineSegment(sketch, "E83.top", {"start": v(1026.4, -21.62) * mm, "end": v(1341.4, -21.62) * mm});
            skLineSegment(sketch, "E83.left", {"start": v(1026.4, 293.38) * mm, "end": v(1026.4, -21.62) * mm});
            skLineSegment(sketch, "E83.right", {"start": v(1341.4, 293.38) * mm, "end": v(1341.4, -21.62) * mm});
            skSolve(sketch);
        }
        {
            var Q0;
            Q0 = qSketchRegion(id + "F136", true);
            extrude(context, id + "F137", {"entities" : qUnion([Q0]), "depth" : 10 * mm, "offsetDistance" : 25 * mm});
        }
        {
            var Q0;
            Q0=qCreatedBy(makeId("Front.planeOp"),FACE);
            var sketch = newSketch(context, id + "F138", { "sketchPlane" : qUnion([Q0])});
            skLineSegment(sketch, "E84.bottom", {"start": v(967.54, -216.56) * mm, "end": v(1377.54, -216.56) * mm});
            skLineSegment(sketch, "E84.top", {"start": v(967.54, -526.56) * mm, "end": v(1377.54, -526.56) * mm});
            skLineSegment(sketch, "E84.left", {"start": v(967.54, -216.56) * mm, "end": v(967.54, -526.56) * mm});
            skLineSegment(sketch, "E84.right", {"start": v(1377.54, -216.56) * mm, "end": v(1377.54, -526.56) * mm});
            skSolve(sketch);
        }
        {
            var Q0;
            Q0 = qSketchRegion(id + "F138", true);
            extrude(context, id + "F139", {"entities" : qUnion([Q0]), "depth" : 25 * mm, "offsetDistance" : 25 * mm});
        }
        {
            var Q0;
            Q0=qCreatedBy(makeId("Front.planeOp"),FACE);
            var sketch = newSketch(context, id + "F140", { "sketchPlane" : qUnion([Q0])});
            skLineSegment(sketch, "E85.bottom", {"start": v(1041.22, -852.8) * mm, "end": v(1241.22, -852.8) * mm});
            skLineSegment(sketch, "E85.top", {"start": v(1041.22, -1132.8) * mm, "end": v(1241.22, -1132.8) * mm});
            skLineSegment(sketch, "E85.left", {"start": v(1041.22, -852.8) * mm, "end": v(1041.22, -1132.8) * mm});
            skLineSegment(sketch, "E85.right", {"start": v(1241.22, -852.8) * mm, "end": v(1241.22, -1132.8) * mm});
            skSolve(sketch);
        }
        {
            var Q0;
            Q0 = qSketchRegion(id + "F140", true);
            extrude(context, id + "F141", {"entities" : qUnion([Q0]), "depth" : 100 * mm, "offsetDistance" : 25 * mm});
        }
        {
            var Q0;
            Q0=qCreatedBy(makeId("Front.planeOp"),FACE);
            var sketch = newSketch(context, id + "F142", { "sketchPlane" : qUnion([Q0])});
            skLineSegment(sketch, "E86.bottom", {"start": v(1345.3, -848.53) * mm, "end": v(1645.3, -848.53) * mm});
            skLineSegment(sketch, "E86.top", {"start": v(1345.3, -1048.53) * mm, "end": v(1645.3, -1048.53) * mm});
            skLineSegment(sketch, "E86.left", {"start": v(1345.3, -848.53) * mm, "end": v(1345.3, -1048.53) * mm});
            skLineSegment(sketch, "E86.right", {"start": v(1645.3, -848.53) * mm, "end": v(1645.3, -1048.53) * mm});
            skSolve(sketch);
        }
        {
            var Q0;
            Q0 = qSketchRegion(id + "F142", true);
            extrude(context, id + "F143", {"entities" : qUnion([Q0]), "depth" : 100 * mm, "offsetDistance" : 25 * mm});
        }
        {
            var Q0;
            Q0=qCreatedBy(makeId("Front.planeOp"),FACE);
            var sketch = newSketch(context, id + "F144", { "sketchPlane" : qUnion([Q0])});
            skLineSegment(sketch, "E87.bottom", {"start": v(1253.56, -565.8) * mm, "end": v(1533.56, -565.8) * mm});
            skLineSegment(sketch, "E87.top", {"start": v(1253.56, -765.8) * mm, "end": v(1533.56, -765.8) * mm});
            skLineSegment(sketch, "E87.left", {"start": v(1253.56, -565.8) * mm, "end": v(1253.56, -765.8) * mm});
            skLineSegment(sketch, "E87.right", {"start": v(1533.56, -565.8) * mm, "end": v(1533.56, -765.8) * mm});
            skSolve(sketch);
        }
        {
            var Q0;
            Q0 = qSketchRegion(id + "F144", true);
            extrude(context, id + "F145", {"entities" : qUnion([Q0]), "depth" : 220 * mm, "offsetDistance" : 25 * mm});
        }
        {
            var Q0;
            Q0=qCreatedBy(makeId("Front.planeOp"),FACE);
            var sketch = newSketch(context, id + "F146", { "sketchPlane" : qUnion([Q0])});
            skLineSegment(sketch, "E88.bottom", {"start": v(1500.17, 436.01) * mm, "end": v(2000.17, 436.01) * mm});
            skLineSegment(sketch, "E88.top", {"start": v(1500.17, -163.99) * mm, "end": v(2000.17, -163.99) * mm});
            skLineSegment(sketch, "E88.left", {"start": v(1500.17, 436.01) * mm, "end": v(1500.17, -163.99) * mm});
            skLineSegment(sketch, "E88.right", {"start": v(2000.17, 436.01) * mm, "end": v(2000.17, -163.99) * mm});
            skSolve(sketch);
        }
        {
            var Q0;
            Q0 = qSketchRegion(id + "F146", true);
            extrude(context, id + "F147", {"entities" : qUnion([Q0]), "depth" : 250 * mm, "offsetDistance" : 25 * mm});
        }
        {
            var Q0;
            Q0=qCreatedBy(makeId("Front.planeOp"),FACE);
            var sketch = newSketch(context, id + "F148", { "sketchPlane" : qUnion([Q0])});
            skLineSegment(sketch, "E89.bottom", {"start": v(1634.72, -204.1) * mm, "end": v(1934.72, -204.1) * mm});
            skLineSegment(sketch, "E89.top", {"start": v(1634.72, -684.1) * mm, "end": v(1934.72, -684.1) * mm});
            skLineSegment(sketch, "E89.left", {"start": v(1634.72, -204.1) * mm, "end": v(1634.72, -684.1) * mm});
            skLineSegment(sketch, "E89.right", {"start": v(1934.72, -204.1) * mm, "end": v(1934.72, -684.1) * mm});
            skSolve(sketch);
        }
        {
            var Q0;
            Q0 = qSketchRegion(id + "F148", true);
            extrude(context, id + "F149", {"entities" : qUnion([Q0]), "depth" : 30 * mm, "offsetDistance" : 25 * mm});
        }
        {
            var Q0;
            Q0=qCreatedBy(makeId("Front.planeOp"),FACE);
            var sketch = newSketch(context, id + "F150", { "sketchPlane" : qUnion([Q0])});
            skLineSegment(sketch, "E90.bottom", {"start": v(877.37, -1127.66) * mm, "end": v(1227.37, -1127.66) * mm});
            skLineSegment(sketch, "E90.top", {"start": v(877.37, -1477.66) * mm, "end": v(1227.37, -1477.66) * mm});
            skLineSegment(sketch, "E90.left", {"start": v(877.37, -1127.66) * mm, "end": v(877.37, -1477.66) * mm});
            skLineSegment(sketch, "E90.right", {"start": v(1227.37, -1127.66) * mm, "end": v(1227.37, -1477.66) * mm});
            skSolve(sketch);
        }
        {
            var Q0;
            Q0 = qSketchRegion(id + "F150", true);
            extrude(context, id + "F151", {"entities" : qUnion([Q0]), "depth" : 250 * mm, "offsetDistance" : 25 * mm});
        }
        {
            var Q0;
            Q0=qCreatedBy(makeId("Front.planeOp"),FACE);
            var sketch = newSketch(context, id + "F152", { "sketchPlane" : qUnion([Q0])});
            skLineSegment(sketch, "E91.bottom", {"start": v(0, -1490.5) * mm, "end": v(500, -1490.5) * mm});
            skLineSegment(sketch, "E91.top", {"start": v(0, -1750.5) * mm, "end": v(500, -1750.5) * mm});
            skLineSegment(sketch, "E91.left", {"start": v(0, -1490.5) * mm, "end": v(0, -1750.5) * mm});
            skLineSegment(sketch, "E91.right", {"start": v(500, -1490.5) * mm, "end": v(500, -1750.5) * mm});
            skSolve(sketch);
        }
        {
            var Q0;
            Q0 = qSketchRegion(id + "F152", true);
            extrude(context, id + "F153", {"entities" : qUnion([Q0]), "depth" : 250 * mm, "offsetDistance" : 25 * mm});
        }
        {
            var Q0;
            Q0=qCreatedBy(makeId("Front.planeOp"),FACE);
            var sketch = newSketch(context, id + "F154", { "sketchPlane" : qUnion([Q0])});
            skLineSegment(sketch, "E92.bottom", {"start": v(-783.98, -1545.75) * mm, "end": v(-723.98, -1545.75) * mm});
            skLineSegment(sketch, "E92.top", {"start": v(-783.98, -1755.75) * mm, "end": v(-723.98, -1755.75) * mm});
            skLineSegment(sketch, "E92.left", {"start": v(-783.98, -1545.75) * mm, "end": v(-783.98, -1755.75) * mm});
            skLineSegment(sketch, "E92.right", {"start": v(-723.98, -1545.75) * mm, "end": v(-723.98, -1755.75) * mm});
            skLineSegment(sketch, "E93.0.1.0", {"start": v(-783.98, -1515.75) * mm, "end": v(-723.98, -1515.75) * mm});
            skLineSegment(sketch, "E93.0.1.1", {"start": v(-783.98, -1305.75) * mm, "end": v(-723.98, -1305.75) * mm});
            skLineSegment(sketch, "E93.0.1.2", {"start": v(-723.98, -1305.75) * mm, "end": v(-723.98, -1515.75) * mm});
            skLineSegment(sketch, "E93.0.1.3", {"start": v(-783.98, -1305.75) * mm, "end": v(-783.98, -1515.75) * mm});
            skLineSegment(sketch, "E93.1.0.0", {"start": v(-713.98, -1755.75) * mm, "end": v(-653.98, -1755.75) * mm});
            skLineSegment(sketch, "E93.1.0.1", {"start": v(-713.98, -1545.75) * mm, "end": v(-653.98, -1545.75) * mm});
            skLineSegment(sketch, "E93.1.0.2", {"start": v(-653.98, -1545.75) * mm, "end": v(-653.98, -1755.75) * mm});
            skLineSegment(sketch, "E93.1.0.3", {"start": v(-713.98, -1545.75) * mm, "end": v(-713.98, -1755.75) * mm});
            skLineSegment(sketch, "E93.1.1.0", {"start": v(-713.98, -1515.75) * mm, "end": v(-653.98, -1515.75) * mm});
            skLineSegment(sketch, "E93.1.1.1", {"start": v(-713.98, -1305.75) * mm, "end": v(-653.98, -1305.75) * mm});
            skLineSegment(sketch, "E93.1.1.2", {"start": v(-653.98, -1305.75) * mm, "end": v(-653.98, -1515.75) * mm});
            skLineSegment(sketch, "E93.1.1.3", {"start": v(-713.98, -1305.75) * mm, "end": v(-713.98, -1515.75) * mm});
            skLineSegment(sketch, "E93.2.0.0", {"start": v(-643.98, -1755.75) * mm, "end": v(-583.98, -1755.75) * mm});
            skLineSegment(sketch, "E93.2.0.1", {"start": v(-643.98, -1545.75) * mm, "end": v(-583.98, -1545.75) * mm});
            skLineSegment(sketch, "E93.2.0.2", {"start": v(-583.98, -1545.75) * mm, "end": v(-583.98, -1755.75) * mm});
            skLineSegment(sketch, "E93.2.0.3", {"start": v(-643.98, -1545.75) * mm, "end": v(-643.98, -1755.75) * mm});
            skLineSegment(sketch, "E93.2.1.0", {"start": v(-643.98, -1515.75) * mm, "end": v(-583.98, -1515.75) * mm});
            skLineSegment(sketch, "E93.2.1.1", {"start": v(-643.98, -1305.75) * mm, "end": v(-583.98, -1305.75) * mm});
            skLineSegment(sketch, "E93.2.1.2", {"start": v(-583.98, -1305.75) * mm, "end": v(-583.98, -1515.75) * mm});
            skLineSegment(sketch, "E93.2.1.3", {"start": v(-643.98, -1305.75) * mm, "end": v(-643.98, -1515.75) * mm});
            skLineSegment(sketch, "E93.3.0.0", {"start": v(-573.98, -1755.75) * mm, "end": v(-513.98, -1755.75) * mm});
            skLineSegment(sketch, "E93.3.0.1", {"start": v(-573.98, -1545.75) * mm, "end": v(-513.98, -1545.75) * mm});
            skLineSegment(sketch, "E93.3.0.2", {"start": v(-513.98, -1545.75) * mm, "end": v(-513.98, -1755.75) * mm});
            skLineSegment(sketch, "E93.3.0.3", {"start": v(-573.98, -1545.75) * mm, "end": v(-573.98, -1755.75) * mm});
            skLineSegment(sketch, "E93.3.1.0", {"start": v(-573.98, -1515.75) * mm, "end": v(-513.98, -1515.75) * mm});
            skLineSegment(sketch, "E93.3.1.1", {"start": v(-573.98, -1305.75) * mm, "end": v(-513.98, -1305.75) * mm});
            skLineSegment(sketch, "E93.3.1.2", {"start": v(-513.98, -1305.75) * mm, "end": v(-513.98, -1515.75) * mm});
            skLineSegment(sketch, "E93.3.1.3", {"start": v(-573.98, -1305.75) * mm, "end": v(-573.98, -1515.75) * mm});
            skLineSegment(sketch, "E93.4.0.0", {"start": v(-503.98, -1755.75) * mm, "end": v(-443.98, -1755.75) * mm});
            skLineSegment(sketch, "E93.4.0.1", {"start": v(-503.98, -1545.75) * mm, "end": v(-443.98, -1545.75) * mm});
            skLineSegment(sketch, "E93.4.0.2", {"start": v(-443.98, -1545.75) * mm, "end": v(-443.98, -1755.75) * mm});
            skLineSegment(sketch, "E93.4.0.3", {"start": v(-503.98, -1545.75) * mm, "end": v(-503.98, -1755.75) * mm});
            skLineSegment(sketch, "E93.4.1.0", {"start": v(-503.98, -1515.75) * mm, "end": v(-443.98, -1515.75) * mm});
            skLineSegment(sketch, "E93.4.1.1", {"start": v(-503.98, -1305.75) * mm, "end": v(-443.98, -1305.75) * mm});
            skLineSegment(sketch, "E93.4.1.2", {"start": v(-443.98, -1305.75) * mm, "end": v(-443.98, -1515.75) * mm});
            skLineSegment(sketch, "E93.4.1.3", {"start": v(-503.98, -1305.75) * mm, "end": v(-503.98, -1515.75) * mm});
            skLineSegment(sketch, "E93.5.0.0", {"start": v(-433.98, -1755.75) * mm, "end": v(-373.98, -1755.75) * mm});
            skLineSegment(sketch, "E93.5.0.1", {"start": v(-433.98, -1545.75) * mm, "end": v(-373.98, -1545.75) * mm});
            skLineSegment(sketch, "E93.5.0.2", {"start": v(-373.98, -1545.75) * mm, "end": v(-373.98, -1755.75) * mm});
            skLineSegment(sketch, "E93.5.0.3", {"start": v(-433.98, -1545.75) * mm, "end": v(-433.98, -1755.75) * mm});
            skLineSegment(sketch, "E93.5.1.0", {"start": v(-433.98, -1515.75) * mm, "end": v(-373.98, -1515.75) * mm});
            skLineSegment(sketch, "E93.5.1.1", {"start": v(-433.98, -1305.75) * mm, "end": v(-373.98, -1305.75) * mm});
            skLineSegment(sketch, "E93.5.1.2", {"start": v(-373.98, -1305.75) * mm, "end": v(-373.98, -1515.75) * mm});
            skLineSegment(sketch, "E93.5.1.3", {"start": v(-433.98, -1305.75) * mm, "end": v(-433.98, -1515.75) * mm});
            skLineSegment(sketch, "E93.direction1", {"start": v(-783.98, -1755.75) * mm, "end": v(-713.98, -1755.75) * mm, "construction": true});
            skLineSegment(sketch, "E93.direction2", {"start": v(-783.98, -1755.75) * mm, "end": v(-783.98, -1515.75) * mm, "construction": true});
            skSolve(sketch);
        }
        {
            var Q0;
            Q0 = qSketchRegion(id + "F154", true);
            extrude(context, id + "F155", {"entities" : qUnion([Q0]), "depth" : 60 * mm, "offsetDistance" : 25 * mm});
        }
        {
            var Q0;
            Q0=qCreatedBy(makeId("Front.planeOp"),FACE);
            var sketch = newSketch(context, id + "F156", { "sketchPlane" : qUnion([Q0])});
            skLineSegment(sketch, "E94.bottom", {"start": v(-1439.33, -1341.58) * mm, "end": v(-1089.33, -1341.58) * mm});
            skLineSegment(sketch, "E94.top", {"start": v(-1439.33, -1791.58) * mm, "end": v(-1089.33, -1791.58) * mm});
            skLineSegment(sketch, "E94.left", {"start": v(-1439.33, -1341.58) * mm, "end": v(-1439.33, -1791.58) * mm});
            skLineSegment(sketch, "E94.right", {"start": v(-1089.33, -1341.58) * mm, "end": v(-1089.33, -1791.58) * mm});
            skSolve(sketch);
        }
        {
            var Q0;
            Q0 = qSketchRegion(id + "F156", true);
            extrude(context, id + "F157", {"entities" : qUnion([Q0]), "depth" : 350 * mm, "offsetDistance" : 25 * mm});
        }
        {
            var Q0;
            Q0=qCreatedBy(makeId("Front.planeOp"),FACE);
            var sketch = newSketch(context, id + "F158", { "sketchPlane" : qUnion([Q0])});
            skCircle(sketch, "E95", {"center": v(-1873.7, -1547.83) * mm, "radius": 167.5 * mm});
            skSolve(sketch);
        }
        {
            var Q0;
            Q0 = qSketchRegion(id + "F158", true);
            extrude(context, id + "F159", {"entities" : qUnion([Q0]), "depth" : 25 * mm, "offsetDistance" : 25 * mm});
        }
        {
            var Q0;
            Q0=makeQuery(id+"F159.opExtrude","CAP_FACE",FACE,{"disambiguationData":[OSD([sQuery(id+"F158.wireOp",EDGE,"E95")])],"isStart":false});
            var sketch = newSketch(context, id + "F160", { "sketchPlane" : qUnion([Q0])});
            skLineSegment(sketch, "E96.bottom", {"start": v(-2071.27, -1346.27) * mm, "end": v(-1771.27, -1346.27) * mm});
            skLineSegment(sketch, "E96.top", {"start": v(-2071.27, -1496.27) * mm, "end": v(-1771.27, -1496.27) * mm});
            skLineSegment(sketch, "E96.left", {"start": v(-2071.27, -1346.27) * mm, "end": v(-2071.27, -1496.27) * mm});
            skLineSegment(sketch, "E96.right", {"start": v(-1771.27, -1346.27) * mm, "end": v(-1771.27, -1496.27) * mm});
            skSolve(sketch);
        }
        {
            var Q0;
            Q0 = qSketchRegion(id + "F160", true);
            extrude(context, id + "F161", {"entities" : qUnion([Q0]), "depth" : 10 * mm, "offsetDistance" : 25 * mm});
        }
        {
            var Q0;
            Q0=makeQuery(id+"F159.opExtrude","CAP_FACE",FACE,{"disambiguationData":[OSD([sQuery(id+"F158.wireOp",EDGE,"E95")])],"isStart":false});
            var sketch = newSketch(context, id + "F162", { "sketchPlane" : qUnion([Q0])});
            skLineSegment(sketch, "E97.bottom", {"start": v(-2144.33, -1583.84) * mm, "end": v(-1844.33, -1583.84) * mm});
            skLineSegment(sketch, "E97.top", {"start": v(-2144.33, -1733.84) * mm, "end": v(-1844.33, -1733.84) * mm});
            skLineSegment(sketch, "E97.left", {"start": v(-2144.33, -1583.84) * mm, "end": v(-2144.33, -1733.84) * mm});
            skLineSegment(sketch, "E97.right", {"start": v(-1844.33, -1583.84) * mm, "end": v(-1844.33, -1733.84) * mm});
            skSolve(sketch);
        }
        {
            var Q0;
            {var subQ1=sQuery(id+"F162.wireOp",EDGE,"E97.top");Q0=makeQuery(id+"F162.imprint","IMPRINT",FACE,{"disambiguationData":[TD([[makeQuery(id+"F162.imprint","IMPRINT",EDGE,{"derivedFrom":subQ1}),1.0]])]});}
            var Q1;
            {var subQ0=sQuery(id+"F162.wireOp",EDGE,"E97.right");var subQ1=sQuery(id+"F162.wireOp",EDGE,"E97.bottom");var subQ2=makeQuery(id+"F162.imprint","INTERSECT",VERTEX,{"derivedFrom":[subQ1,subQ0]});Q1=makeQuery(id+"F162.imprint","IMPRINT",FACE,{"disambiguationData":[TD([[makeQuery(id+"F162.imprint","IMPRINT",EDGE,{"disambiguationData":[TD([[subQ2,1.0]])],"derivedFrom":subQ1}),-1.0]])]});}
            extrude(context, id + "F163", {"entities" : qUnion([Q0, Q1]), "depth" : 10 * mm, "offsetDistance" : 25 * mm});
        }
        {
            var Q0;
            Q0=qCreatedBy(makeId("Front.planeOp"),FACE);
            var sketch = newSketch(context, id + "F164", { "sketchPlane" : qUnion([Q0])});
            skLineSegment(sketch, "E98.bottom", {"start": v(-2546.81, -1475.03) * mm, "end": v(-2266.81, -1475.03) * mm});
            skLineSegment(sketch, "E98.top", {"start": v(-2546.81, -1625.03) * mm, "end": v(-2266.81, -1625.03) * mm});
            skLineSegment(sketch, "E98.left", {"start": v(-2546.81, -1475.03) * mm, "end": v(-2546.81, -1625.03) * mm});
            skLineSegment(sketch, "E98.right", {"start": v(-2266.81, -1475.03) * mm, "end": v(-2266.81, -1625.03) * mm});
            skSolve(sketch);
        }
        {
            var Q0;
            Q0 = qSketchRegion(id + "F164", true);
            extrude(context, id + "F165", {"entities" : qUnion([Q0]), "depth" : 100 * mm, "offsetDistance" : 25 * mm});
        }
        {
            var Q0;
            Q0=qCreatedBy(makeId("Front.planeOp"),FACE);
            var sketch = newSketch(context, id + "F166", { "sketchPlane" : qUnion([Q0])});
            skLineSegment(sketch, "E99.bottom", {"start": v(-3070.5, -1480.06) * mm, "end": v(-2830.5, -1480.06) * mm});
            skLineSegment(sketch, "E99.top", {"start": v(-3070.5, -1630.06) * mm, "end": v(-2830.5, -1630.06) * mm});
            skLineSegment(sketch, "E99.left", {"start": v(-3070.5, -1480.06) * mm, "end": v(-3070.5, -1630.06) * mm});
            skLineSegment(sketch, "E99.right", {"start": v(-2830.5, -1480.06) * mm, "end": v(-2830.5, -1630.06) * mm});
            skSolve(sketch);
        }
        {
            var Q0;
            Q0 = qSketchRegion(id + "F166", true);
            extrude(context, id + "F167", {"entities" : qUnion([Q0]), "depth" : 190 * mm, "offsetDistance" : 25 * mm});
        }
        {
            var Q0;
            Q0=qCreatedBy(makeId("Front.planeOp"),FACE);
            var sketch = newSketch(context, id + "F168", { "sketchPlane" : qUnion([Q0])});
            skLineSegment(sketch, "E100.bottom", {"start": v(-2846.7, -1621.77) * mm, "end": v(-2681.7, -1621.77) * mm});
            skLineSegment(sketch, "E100.top", {"start": v(-2846.7, -1771.77) * mm, "end": v(-2681.7, -1771.77) * mm});
            skLineSegment(sketch, "E100.left", {"start": v(-2846.7, -1621.77) * mm, "end": v(-2846.7, -1771.77) * mm});
            skLineSegment(sketch, "E100.right", {"start": v(-2681.7, -1621.77) * mm, "end": v(-2681.7, -1771.77) * mm});
            skSolve(sketch);
        }
        {
            var Q0;
            Q0 = qSketchRegion(id + "F168", true);
            extrude(context, id + "F169", {"entities" : qUnion([Q0]), "depth" : 30 * mm, "offsetDistance" : 25 * mm});
        }
        {
            var Q0;
            Q0=qCreatedBy(makeId("Front.planeOp"),FACE);
            var sketch = newSketch(context, id + "F170", { "sketchPlane" : qUnion([Q0])});
            skCircle(sketch, "E101", {"center": v(-3005.13, -1735.81) * mm, "radius": 80 * mm});
            skSolve(sketch);
        }
        {
            var Q0;
            Q0 = qSketchRegion(id + "F170", true);
            extrude(context, id + "F171", {"entities" : qUnion([Q0]), "depth" : 160 * mm, "offsetDistance" : 25 * mm});
        }
        {
            var Q0;
            Q0=qCreatedBy(makeId("Front.planeOp"),FACE);
            var sketch = newSketch(context, id + "F172", { "sketchPlane" : qUnion([Q0])});
            skLineSegment(sketch, "E102.bottom", {"start": v(-3693.78, -852.84) * mm, "end": v(-3193.78, -852.84) * mm});
            skLineSegment(sketch, "E102.top", {"start": v(-3693.78, -1622.84) * mm, "end": v(-3193.78, -1622.84) * mm});
            skLineSegment(sketch, "E102.left", {"start": v(-3693.78, -852.84) * mm, "end": v(-3693.78, -1622.84) * mm});
            skLineSegment(sketch, "E102.right", {"start": v(-3193.78, -852.84) * mm, "end": v(-3193.78, -1622.84) * mm});
            skSolve(sketch);
        }
        {
            var Q0;
            Q0 = qSketchRegion(id + "F172", true);
            extrude(context, id + "F173", {"entities" : qUnion([Q0]), "depth" : 150 * mm, "offsetDistance" : 25 * mm});
        }
        {
            var Q0;
            Q0=qCreatedBy(makeId("Front.planeOp"),FACE);
            var sketch = newSketch(context, id + "F174", { "sketchPlane" : qUnion([Q0])});
            skLineSegment(sketch, "E103.bottom", {"start": v(1372.39, -1334) * mm, "end": v(1722.39, -1334) * mm});
            skLineSegment(sketch, "E103.top", {"start": v(1372.39, -1574) * mm, "end": v(1722.39, -1574) * mm});
            skLineSegment(sketch, "E103.left", {"start": v(1372.39, -1334) * mm, "end": v(1372.39, -1574) * mm});
            skLineSegment(sketch, "E103.right", {"start": v(1722.39, -1334) * mm, "end": v(1722.39, -1574) * mm});
            skSolve(sketch);
        }
        {
            var Q0;
            Q0 = qSketchRegion(id + "F174", true);
            extrude(context, id + "F175", {"entities" : qUnion([Q0]), "depth" : 170 * mm, "offsetDistance" : 25 * mm});
        }
        {
            var Q0;
            Q0=qCreatedBy(makeId("Front.planeOp"),FACE);
            var sketch = newSketch(context, id + "F176", { "sketchPlane" : qUnion([Q0])});
            skLineSegment(sketch, "E104.bottom", {"start": v(790.65, -1521.5) * mm, "end": v(1040.65, -1521.5) * mm});
            skLineSegment(sketch, "E104.top", {"start": v(790.65, -1741.5) * mm, "end": v(1040.65, -1741.5) * mm});
            skLineSegment(sketch, "E104.left", {"start": v(790.65, -1521.5) * mm, "end": v(790.65, -1741.5) * mm});
            skLineSegment(sketch, "E104.right", {"start": v(1040.65, -1521.5) * mm, "end": v(1040.65, -1741.5) * mm});
            skSolve(sketch);
        }
        {
            var Q0;
            Q0 = qSketchRegion(id + "F176", true);
            extrude(context, id + "F177", {"entities" : qUnion([Q0]), "depth" : 50 * mm, "offsetDistance" : 25 * mm});
        }
        {
            var Q0;
            Q0=qCreatedBy(makeId("Front.planeOp"),FACE);
            var sketch = newSketch(context, id + "F178", { "sketchPlane" : qUnion([Q0])});
            skLineSegment(sketch, "E105.bottom", {"start": v(1722.7, -780.95) * mm, "end": v(1912.7, -780.95) * mm});
            skLineSegment(sketch, "E105.top", {"start": v(1722.7, -1030.95) * mm, "end": v(1912.7, -1030.95) * mm});
            skLineSegment(sketch, "E105.left", {"start": v(1722.7, -780.95) * mm, "end": v(1722.7, -1030.95) * mm});
            skLineSegment(sketch, "E105.right", {"start": v(1912.7, -780.95) * mm, "end": v(1912.7, -1030.95) * mm});
            skSolve(sketch);
        }
        {
            var Q0;
            Q0 = qSketchRegion(id + "F178", true);
            extrude(context, id + "F179", {"entities" : qUnion([Q0]), "depth" : 60 * mm, "offsetDistance" : 25 * mm});
        }
        {
            var Q0;
            Q0=qCreatedBy(makeId("Front.planeOp"),FACE);
            var sketch = newSketch(context, id + "F180", { "sketchPlane" : qUnion([Q0])});
            skLineSegment(sketch, "E106.bottom", {"start": v(1654.74, -801.35) * mm, "end": v(1964.74, -801.35) * mm});
            skLineSegment(sketch, "E106.top", {"start": v(1654.74, -1261.35) * mm, "end": v(1964.74, -1261.35) * mm});
            skLineSegment(sketch, "E106.left", {"start": v(1654.74, -801.35) * mm, "end": v(1654.74, -1261.35) * mm});
            skLineSegment(sketch, "E106.right", {"start": v(1964.74, -801.35) * mm, "end": v(1964.74, -1261.35) * mm});
            skSolve(sketch);
        }
        {
            var Q0;
            Q0 = qSketchRegion(id + "F180", true);
            extrude(context, id + "F181", {"entities" : qUnion([Q0]), "depth" : 50 * mm, "offsetDistance" : 25 * mm});
        }
        {
            var Q0;
            Q0=qCreatedBy(makeId("Front.planeOp"),FACE);
            var sketch = newSketch(context, id + "F182", { "sketchPlane" : qUnion([Q0])});
            skLineSegment(sketch, "E107.bottom", {"start": v(-4085.68, -1144.29) * mm, "end": v(-3785.68, -1144.29) * mm});
            skLineSegment(sketch, "E107.top", {"start": v(-4085.68, -1644.29) * mm, "end": v(-3785.68, -1644.29) * mm});
            skLineSegment(sketch, "E107.left", {"start": v(-4085.68, -1144.29) * mm, "end": v(-4085.68, -1644.29) * mm});
            skLineSegment(sketch, "E107.right", {"start": v(-3785.68, -1144.29) * mm, "end": v(-3785.68, -1644.29) * mm});
            skSolve(sketch);
        }
        {
            var Q0;
            Q0 = qSketchRegion(id + "F182", true);
            extrude(context, id + "F183", {"entities" : qUnion([Q0]), "depth" : 110 * mm, "offsetDistance" : 25 * mm});
        }
        {
            var Q0;
            Q0=qCreatedBy(makeId("Front.planeOp"),FACE);
            var sketch = newSketch(context, id + "F184", { "sketchPlane" : qUnion([Q0])});
            skLineSegment(sketch, "E108.bottom", {"start": v(1357.13, -1677.5) * mm, "end": v(1442.13, -1677.5) * mm});
            skLineSegment(sketch, "E108.top", {"start": v(1357.13, -1817.5) * mm, "end": v(1442.13, -1817.5) * mm});
            skLineSegment(sketch, "E108.left", {"start": v(1357.13, -1677.5) * mm, "end": v(1357.13, -1817.5) * mm});
            skLineSegment(sketch, "E108.right", {"start": v(1442.13, -1677.5) * mm, "end": v(1442.13, -1817.5) * mm});
            skLineSegment(sketch, "E109.0.1.0", {"start": v(1357.13, -1517.5) * mm, "end": v(1442.13, -1517.5) * mm});
            skLineSegment(sketch, "E109.0.1.1", {"start": v(1357.13, -1517.5) * mm, "end": v(1357.13, -1657.5) * mm});
            skLineSegment(sketch, "E109.0.1.2", {"start": v(1357.13, -1657.5) * mm, "end": v(1442.13, -1657.5) * mm});
            skLineSegment(sketch, "E109.0.1.3", {"start": v(1442.13, -1517.5) * mm, "end": v(1442.13, -1657.5) * mm});
            skLineSegment(sketch, "E109.1.0.0", {"start": v(1462.13, -1677.5) * mm, "end": v(1547.13, -1677.5) * mm});
            skLineSegment(sketch, "E109.1.0.1", {"start": v(1462.13, -1677.5) * mm, "end": v(1462.13, -1817.5) * mm});
            skLineSegment(sketch, "E109.1.0.2", {"start": v(1462.13, -1817.5) * mm, "end": v(1547.13, -1817.5) * mm});
            skLineSegment(sketch, "E109.1.0.3", {"start": v(1547.13, -1677.5) * mm, "end": v(1547.13, -1817.5) * mm});
            skLineSegment(sketch, "E109.1.1.0", {"start": v(1462.13, -1517.5) * mm, "end": v(1547.13, -1517.5) * mm});
            skLineSegment(sketch, "E109.1.1.1", {"start": v(1462.13, -1517.5) * mm, "end": v(1462.13, -1657.5) * mm});
            skLineSegment(sketch, "E109.1.1.2", {"start": v(1462.13, -1657.5) * mm, "end": v(1547.13, -1657.5) * mm});
            skLineSegment(sketch, "E109.1.1.3", {"start": v(1547.13, -1517.5) * mm, "end": v(1547.13, -1657.5) * mm});
            skLineSegment(sketch, "E109.2.0.0", {"start": v(1567.13, -1677.5) * mm, "end": v(1652.13, -1677.5) * mm});
            skLineSegment(sketch, "E109.2.0.1", {"start": v(1567.13, -1677.5) * mm, "end": v(1567.13, -1817.5) * mm});
            skLineSegment(sketch, "E109.2.0.2", {"start": v(1567.13, -1817.5) * mm, "end": v(1652.13, -1817.5) * mm});
            skLineSegment(sketch, "E109.2.0.3", {"start": v(1652.13, -1677.5) * mm, "end": v(1652.13, -1817.5) * mm});
            skLineSegment(sketch, "E109.2.1.0", {"start": v(1567.13, -1517.5) * mm, "end": v(1652.13, -1517.5) * mm});
            skLineSegment(sketch, "E109.2.1.1", {"start": v(1567.13, -1517.5) * mm, "end": v(1567.13, -1657.5) * mm});
            skLineSegment(sketch, "E109.2.1.2", {"start": v(1567.13, -1657.5) * mm, "end": v(1652.13, -1657.5) * mm});
            skLineSegment(sketch, "E109.2.1.3", {"start": v(1652.13, -1517.5) * mm, "end": v(1652.13, -1657.5) * mm});
            skLineSegment(sketch, "E109.direction1", {"start": v(1357.13, -1817.5) * mm, "end": v(1462.13, -1817.5) * mm, "construction": true});
            skLineSegment(sketch, "E109.direction2", {"start": v(1357.13, -1817.5) * mm, "end": v(1357.13, -1657.5) * mm, "construction": true});
            skSolve(sketch);
        }
        {
            var Q0;
            Q0=makeQuery(id+"F184.imprint","IMPRINT",FACE,{"disambiguationData":[TD([[makeQuery(id+"F184.imprint","IMPRINT",EDGE,{"derivedFrom":sQuery(id+"F184.wireOp",EDGE,"E109.1.0.0")}),-1.0]])]});
            var Q1;
            Q1=makeQuery(id+"F184.imprint","IMPRINT",FACE,{"disambiguationData":[TD([[makeQuery(id+"F184.imprint","IMPRINT",EDGE,{"derivedFrom":sQuery(id+"F184.wireOp",EDGE,"E108.bottom")}),-1.0]])]});
            var Q2;
            Q2=makeQuery(id+"F184.imprint","IMPRINT",FACE,{"disambiguationData":[TD([[makeQuery(id+"F184.imprint","IMPRINT",EDGE,{"derivedFrom":sQuery(id+"F184.wireOp",EDGE,"E109.0.1.0")}),-1.0]])]});
            var Q3;
            Q3=makeQuery(id+"F184.imprint","IMPRINT",FACE,{"disambiguationData":[TD([[makeQuery(id+"F184.imprint","IMPRINT",EDGE,{"derivedFrom":sQuery(id+"F184.wireOp",EDGE,"E109.1.1.0")}),-1.0]])]});
            var Q4;
            Q4=makeQuery(id+"F184.imprint","IMPRINT",FACE,{"disambiguationData":[TD([[makeQuery(id+"F184.imprint","IMPRINT",EDGE,{"derivedFrom":sQuery(id+"F184.wireOp",EDGE,"E109.2.1.0")}),-1.0]])]});
            var Q5;
            Q5=makeQuery(id+"F184.imprint","IMPRINT",FACE,{"disambiguationData":[TD([[makeQuery(id+"F184.imprint","IMPRINT",EDGE,{"derivedFrom":sQuery(id+"F184.wireOp",EDGE,"E109.2.0.0")}),-1.0]])]});
            extrude(context, id + "F185", {"entities" : qUnion([Q0, Q1, Q2, Q3, Q4, Q5]), "depth" : 85 * mm, "offsetDistance" : 25 * mm});
        }
        {
            var Q0;
            Q0=qCreatedBy(makeId("Front.planeOp"),FACE);
            var sketch = newSketch(context, id + "F186", { "sketchPlane" : qUnion([Q0])});
            skLineSegment(sketch, "E110.bottom", {"start": v(576.82, -1916.2) * mm, "end": v(956.82, -1916.2) * mm});
            skLineSegment(sketch, "E110.top", {"start": v(576.82, -2366.2) * mm, "end": v(956.82, -2366.2) * mm});
            skLineSegment(sketch, "E110.left", {"start": v(576.82, -1916.2) * mm, "end": v(576.82, -2366.2) * mm});
            skLineSegment(sketch, "E110.right", {"start": v(956.82, -1916.2) * mm, "end": v(956.82, -2366.2) * mm});
            skSolve(sketch);
        }
        {
            var Q0;
            Q0 = qSketchRegion(id + "F186", true);
            extrude(context, id + "F187", {"entities" : qUnion([Q0]), "depth" : 110 * mm, "offsetDistance" : 25 * mm});
        }
    });
